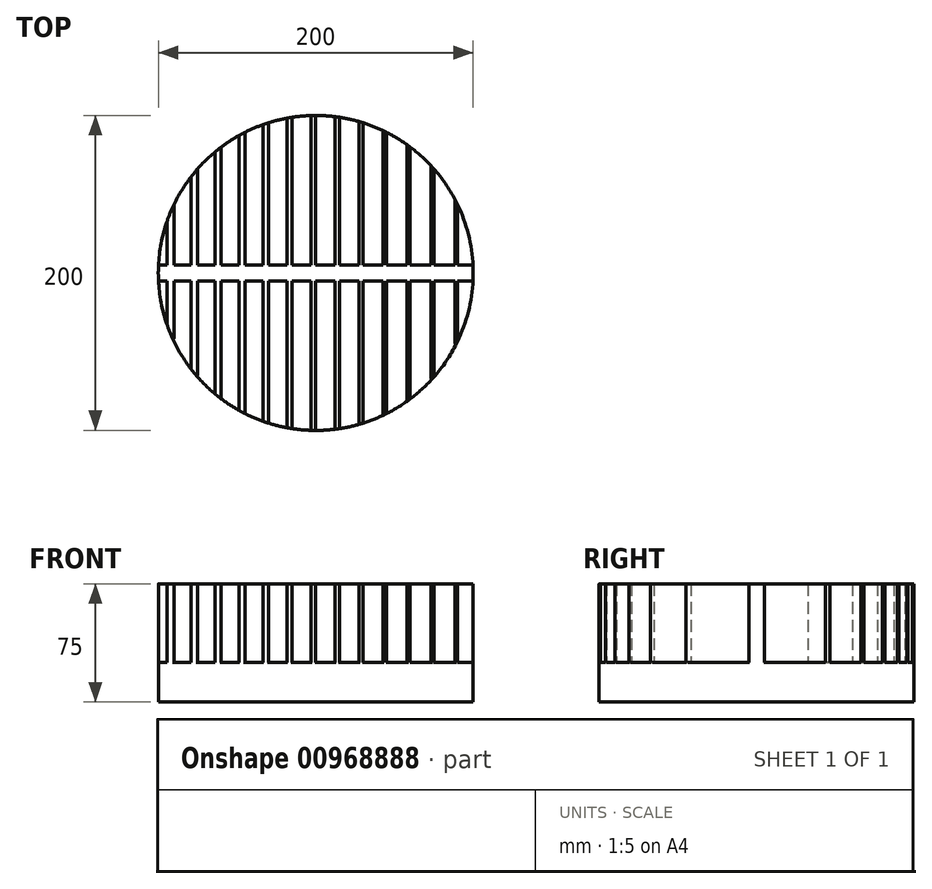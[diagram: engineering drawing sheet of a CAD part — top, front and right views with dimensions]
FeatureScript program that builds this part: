
annotation { "Feature Type Name" : "Feature", "Feature Type Description" : "" }
export const myFeature = defineFeature(function(context is Context, id is Id, definition is map)
    precondition{}
    {
        {
            var Q0;
            Q0=qCreatedBy(makeId("Top.planeOp"),FACE);
            var sketch = newSketch(context, id + "F0", { "sketchPlane" : qUnion([Q0])});
            skCircle(sketch, "E0", {"center": v(0, 0) * mm, "radius": 100 * mm});
            skLineSegment(sketch, "E1", {"start": v(-153.58, 0) * mm, "end": v(193.93, 0) * mm});
            skLineSegment(sketch, "E2", {"start": v(0, 104.63) * mm, "end": v(0, -103.63) * mm});
            skLineSegment(sketch, "E3.1.0.0", {"start": v(15, 104.63) * mm, "end": v(15, -103.63) * mm});
            skLineSegment(sketch, "E3.2.0.0", {"start": v(30, 104.63) * mm, "end": v(30, -103.63) * mm});
            skLineSegment(sketch, "E3.3.0.0", {"start": v(45, 104.63) * mm, "end": v(45, -103.63) * mm});
            skLineSegment(sketch, "E3.4.0.0", {"start": v(60, 104.63) * mm, "end": v(60, -103.63) * mm});
            skLineSegment(sketch, "E3.5.0.0", {"start": v(75, 104.63) * mm, "end": v(75, -103.63) * mm});
            skLineSegment(sketch, "E3.6.0.0", {"start": v(90, 104.63) * mm, "end": v(90, -103.63) * mm});
            skLineSegment(sketch, "E3.direction1", {"start": v(0, -103.63) * mm, "end": v(15, -103.63) * mm, "construction": true});
            skLineSegment(sketch, "E4.MirrorCS", {"start": v(-15, 104.63) * mm, "end": v(-15, -103.63) * mm});
            skLineSegment(sketch, "E5.MirrorCS", {"start": v(-30, 104.63) * mm, "end": v(-30, -103.63) * mm});
            skLineSegment(sketch, "E6.MirrorCS", {"start": v(-45, 104.63) * mm, "end": v(-45, -103.63) * mm});
            skLineSegment(sketch, "E7.MirrorCS", {"start": v(-60, 104.63) * mm, "end": v(-60, -103.63) * mm});
            skLineSegment(sketch, "E8.MirrorCS", {"start": v(-75, 104.63) * mm, "end": v(-75, -103.63) * mm});
            skLineSegment(sketch, "E9.MirrorCS", {"start": v(-90, 104.63) * mm, "end": v(-90, -103.63) * mm});
            skLineSegment(sketch, "E10.0", {"start": v(88.5, 104.63) * mm, "end": v(88.5, -103.63) * mm});
            skLineSegment(sketch, "E11.0", {"start": v(73.25, 104.63) * mm, "end": v(73.25, -103.63) * mm});
            skLineSegment(sketch, "E12.0", {"start": v(58, 104.63) * mm, "end": v(58, -103.63) * mm});
            skLineSegment(sketch, "E13.0", {"start": v(42.75, 104.63) * mm, "end": v(42.75, -103.63) * mm});
            skLineSegment(sketch, "E14.0", {"start": v(27.5, 104.63) * mm, "end": v(27.5, -103.63) * mm});
            skLineSegment(sketch, "E15.0", {"start": v(12.25, 104.63) * mm, "end": v(12.25, -103.63) * mm});
            skLineSegment(sketch, "E16.0", {"start": v(-3, 104.63) * mm, "end": v(-3, -103.63) * mm});
            skLineSegment(sketch, "E17.0", {"start": v(-18.25, 104.63) * mm, "end": v(-18.25, -103.63) * mm});
            skLineSegment(sketch, "E18.0", {"start": v(-33.5, 104.63) * mm, "end": v(-33.5, -103.63) * mm});
            skLineSegment(sketch, "E19.0", {"start": v(-48.75, 104.63) * mm, "end": v(-48.75, -103.63) * mm});
            skLineSegment(sketch, "E20.0", {"start": v(-64, 104.63) * mm, "end": v(-64, -103.63) * mm});
            skLineSegment(sketch, "E21.0", {"start": v(-79.25, 104.63) * mm, "end": v(-79.25, -103.63) * mm});
            skLineSegment(sketch, "E22.0", {"start": v(-94.5, 104.63) * mm, "end": v(-94.5, -103.63) * mm});
            skLineSegment(sketch, "E23.bottom", {"start": v(-150, 5) * mm, "end": v(150, 5) * mm});
            skLineSegment(sketch, "E23.top", {"start": v(-150, -5) * mm, "end": v(150, -5) * mm});
            skLineSegment(sketch, "E23.left", {"start": v(-150, 5) * mm, "end": v(-150, -5) * mm});
            skLineSegment(sketch, "E23.right", {"start": v(150, 5) * mm, "end": v(150, -5) * mm});
            skSolve(sketch);
        }
        {
            var Q0;
            {var subQ0=sQuery(id+"F0.wireOp",EDGE,"E22.0");var subQ1=sQuery(id+"F0.wireOp",EDGE,"E0");var subQ2=makeQuery(id+"F0.imprint","INTERSECT",VERTEX,{"disambiguationData":[OD(1.0)],"derivedFrom":[subQ1,subQ0]});Q0=makeQuery(id+"F0.imprint","IMPRINT",FACE,{"disambiguationData":[TD([[makeQuery(id+"F0.imprint","IMPRINT",EDGE,{"disambiguationData":[TD([[subQ2,1.0]])],"derivedFrom":subQ1}),1.0]])]});}
            var Q1;
            {var subQ0=sQuery(id+"F0.wireOp",EDGE,"E23.top");var subQ1=sQuery(id+"F0.wireOp",EDGE,"E0");var subQ2=makeQuery(id+"F0.imprint","INTERSECT",VERTEX,{"disambiguationData":[OD(0.0)],"derivedFrom":[subQ1,subQ0]});Q1=makeQuery(id+"F0.imprint","IMPRINT",FACE,{"disambiguationData":[TD([[makeQuery(id+"F0.imprint","IMPRINT",EDGE,{"disambiguationData":[TD([[subQ2,1.0]])],"derivedFrom":subQ1}),1.0]])]});}
            var Q2;
            {var subQ0=sQuery(id+"F0.wireOp",EDGE,"E23.bottom");var subQ1=sQuery(id+"F0.wireOp",EDGE,"E0");var subQ2=makeQuery(id+"F0.imprint","INTERSECT",VERTEX,{"disambiguationData":[OD(1.0)],"derivedFrom":[subQ1,subQ0]});Q2=makeQuery(id+"F0.imprint","IMPRINT",FACE,{"disambiguationData":[TD([[makeQuery(id+"F0.imprint","IMPRINT",EDGE,{"disambiguationData":[TD([[subQ2,-1.0]])],"derivedFrom":subQ1}),1.0]])]});}
            var Q3;
            {var subQ0=sQuery(id+"F0.wireOp",EDGE,"E22.0");var subQ1=sQuery(id+"F0.wireOp",EDGE,"E0");var subQ2=makeQuery(id+"F0.imprint","INTERSECT",VERTEX,{"disambiguationData":[OD(0.0)],"derivedFrom":[subQ1,subQ0]});Q3=makeQuery(id+"F0.imprint","IMPRINT",FACE,{"disambiguationData":[TD([[makeQuery(id+"F0.imprint","IMPRINT",EDGE,{"disambiguationData":[TD([[subQ2,-1.0]])],"derivedFrom":subQ1}),1.0]])]});}
            var Q4;
            {var subQ0=sQuery(id+"F0.wireOp",EDGE,"E4.MirrorCS");var subQ1=sQuery(id+"F0.wireOp",EDGE,"E0");var subQ2=makeQuery(id+"F0.imprint","INTERSECT",VERTEX,{"disambiguationData":[OD(1.0)],"derivedFrom":[subQ1,subQ0]});Q4=makeQuery(id+"F0.imprint","IMPRINT",FACE,{"disambiguationData":[TD([[makeQuery(id+"F0.imprint","IMPRINT",EDGE,{"disambiguationData":[TD([[subQ2,-1.0]])],"derivedFrom":subQ1}),1.0]])]});}
            var Q5;
            {var subQ0=sQuery(id+"F0.wireOp",EDGE,"E5.MirrorCS");var subQ1=sQuery(id+"F0.wireOp",EDGE,"E0");var subQ2=makeQuery(id+"F0.imprint","INTERSECT",VERTEX,{"disambiguationData":[OD(0.0)],"derivedFrom":[subQ1,subQ0]});Q5=makeQuery(id+"F0.imprint","IMPRINT",FACE,{"disambiguationData":[TD([[makeQuery(id+"F0.imprint","IMPRINT",EDGE,{"disambiguationData":[TD([[subQ2,-1.0]])],"derivedFrom":subQ1}),1.0]])]});}
            var Q6;
            {var subQ0=sQuery(id+"F0.wireOp",EDGE,"E16.0");var subQ1=sQuery(id+"F0.wireOp",EDGE,"E0");var subQ2=makeQuery(id+"F0.imprint","INTERSECT",VERTEX,{"disambiguationData":[OD(0.0)],"derivedFrom":[subQ1,subQ0]});Q6=makeQuery(id+"F0.imprint","IMPRINT",FACE,{"disambiguationData":[TD([[makeQuery(id+"F0.imprint","IMPRINT",EDGE,{"disambiguationData":[TD([[subQ2,-1.0]])],"derivedFrom":subQ1}),1.0]])]});}
            var Q7;
            {var subQ0=sQuery(id+"F0.wireOp",EDGE,"E15.0");var subQ1=sQuery(id+"F0.wireOp",EDGE,"E0");var subQ2=makeQuery(id+"F0.imprint","INTERSECT",VERTEX,{"disambiguationData":[OD(1.0)],"derivedFrom":[subQ1,subQ0]});Q7=makeQuery(id+"F0.imprint","IMPRINT",FACE,{"disambiguationData":[TD([[makeQuery(id+"F0.imprint","IMPRINT",EDGE,{"disambiguationData":[TD([[subQ2,-1.0]])],"derivedFrom":subQ1}),1.0]])]});}
            var Q8;
            {var subQ0=sQuery(id+"F0.wireOp",EDGE,"E8.MirrorCS");var subQ1=sQuery(id+"F0.wireOp",EDGE,"E1");var subQ2=makeQuery(id+"F0.imprint","INTERSECT",VERTEX,{"derivedFrom":[subQ1,subQ0]});Q8=makeQuery(id+"F0.imprint","IMPRINT",FACE,{"disambiguationData":[TD([[makeQuery(id+"F0.imprint","IMPRINT",EDGE,{"disambiguationData":[TD([[subQ2,-1.0]])],"derivedFrom":subQ1}),-1.0]])]});}
            var Q9;
            {var subQ0=sQuery(id+"F0.wireOp",EDGE,"E17.0");var subQ1=sQuery(id+"F0.wireOp",EDGE,"E0");var subQ2=makeQuery(id+"F0.imprint","INTERSECT",VERTEX,{"disambiguationData":[OD(0.0)],"derivedFrom":[subQ1,subQ0]});Q9=makeQuery(id+"F0.imprint","IMPRINT",FACE,{"disambiguationData":[TD([[makeQuery(id+"F0.imprint","IMPRINT",EDGE,{"disambiguationData":[TD([[subQ2,-1.0]])],"derivedFrom":subQ1}),1.0]])]});}
            var Q10;
            {var subQ0=sQuery(id+"F0.wireOp",EDGE,"E8.MirrorCS");var subQ1=sQuery(id+"F0.wireOp",EDGE,"E1");var subQ2=makeQuery(id+"F0.imprint","INTERSECT",VERTEX,{"derivedFrom":[subQ1,subQ0]});Q10=makeQuery(id+"F0.imprint","IMPRINT",FACE,{"disambiguationData":[TD([[makeQuery(id+"F0.imprint","IMPRINT",EDGE,{"disambiguationData":[TD([[subQ2,1.0]])],"derivedFrom":subQ1}),-1.0]])]});}
            var Q11;
            {var subQ0=sQuery(id+"F0.wireOp",EDGE,"E3.3.0.0");var subQ1=sQuery(id+"F0.wireOp",EDGE,"E0");var subQ2=makeQuery(id+"F0.imprint","INTERSECT",VERTEX,{"disambiguationData":[OD(0.0)],"derivedFrom":[subQ1,subQ0]});Q11=makeQuery(id+"F0.imprint","IMPRINT",FACE,{"disambiguationData":[TD([[makeQuery(id+"F0.imprint","IMPRINT",EDGE,{"disambiguationData":[TD([[subQ2,-1.0]])],"derivedFrom":subQ1}),1.0]])]});}
            var Q12;
            {var subQ0=sQuery(id+"F0.wireOp",EDGE,"E17.0");var subQ1=sQuery(id+"F0.wireOp",EDGE,"E1");var subQ2=makeQuery(id+"F0.imprint","INTERSECT",VERTEX,{"derivedFrom":[subQ1,subQ0]});Q12=makeQuery(id+"F0.imprint","IMPRINT",FACE,{"disambiguationData":[TD([[makeQuery(id+"F0.imprint","IMPRINT",EDGE,{"disambiguationData":[TD([[subQ2,-1.0]])],"derivedFrom":subQ1}),1.0]])]});}
            var Q13;
            {var subQ0=sQuery(id+"F0.wireOp",EDGE,"E13.0");var subQ1=sQuery(id+"F0.wireOp",EDGE,"E0");var subQ2=makeQuery(id+"F0.imprint","INTERSECT",VERTEX,{"disambiguationData":[OD(0.0)],"derivedFrom":[subQ1,subQ0]});Q13=makeQuery(id+"F0.imprint","IMPRINT",FACE,{"disambiguationData":[TD([[makeQuery(id+"F0.imprint","IMPRINT",EDGE,{"disambiguationData":[TD([[subQ2,-1.0]])],"derivedFrom":subQ1}),1.0]])]});}
            var Q14;
            {var subQ0=sQuery(id+"F0.wireOp",EDGE,"E13.0");var subQ1=sQuery(id+"F0.wireOp",EDGE,"E1");var subQ2=makeQuery(id+"F0.imprint","INTERSECT",VERTEX,{"derivedFrom":[subQ1,subQ0]});Q14=makeQuery(id+"F0.imprint","IMPRINT",FACE,{"disambiguationData":[TD([[makeQuery(id+"F0.imprint","IMPRINT",EDGE,{"disambiguationData":[TD([[subQ2,-1.0]])],"derivedFrom":subQ1}),-1.0]])]});}
            var Q15;
            {var subQ0=sQuery(id+"F0.wireOp",EDGE,"E5.MirrorCS");var subQ1=sQuery(id+"F0.wireOp",EDGE,"E1");var subQ2=makeQuery(id+"F0.imprint","INTERSECT",VERTEX,{"derivedFrom":[subQ1,subQ0]});Q15=makeQuery(id+"F0.imprint","IMPRINT",FACE,{"disambiguationData":[TD([[makeQuery(id+"F0.imprint","IMPRINT",EDGE,{"disambiguationData":[TD([[subQ2,1.0]])],"derivedFrom":subQ1}),-1.0]])]});}
            var Q16;
            {var subQ0=sQuery(id+"F0.wireOp",EDGE,"E7.MirrorCS");var subQ1=sQuery(id+"F0.wireOp",EDGE,"E1");var subQ2=makeQuery(id+"F0.imprint","INTERSECT",VERTEX,{"derivedFrom":[subQ1,subQ0]});Q16=makeQuery(id+"F0.imprint","IMPRINT",FACE,{"disambiguationData":[TD([[makeQuery(id+"F0.imprint","IMPRINT",EDGE,{"disambiguationData":[TD([[subQ2,-1.0]])],"derivedFrom":subQ1}),-1.0]])]});}
            var Q17;
            {var subQ0=sQuery(id+"F0.wireOp",EDGE,"E3.2.0.0");var subQ1=sQuery(id+"F0.wireOp",EDGE,"E0");var subQ2=makeQuery(id+"F0.imprint","INTERSECT",VERTEX,{"disambiguationData":[OD(0.0)],"derivedFrom":[subQ1,subQ0]});Q17=makeQuery(id+"F0.imprint","IMPRINT",FACE,{"disambiguationData":[TD([[makeQuery(id+"F0.imprint","IMPRINT",EDGE,{"disambiguationData":[TD([[subQ2,-1.0]])],"derivedFrom":subQ1}),1.0]])]});}
            var Q18;
            {var subQ0=sQuery(id+"F0.wireOp",EDGE,"E15.0");var subQ1=sQuery(id+"F0.wireOp",EDGE,"E0");var subQ2=makeQuery(id+"F0.imprint","INTERSECT",VERTEX,{"disambiguationData":[OD(0.0)],"derivedFrom":[subQ1,subQ0]});Q18=makeQuery(id+"F0.imprint","IMPRINT",FACE,{"disambiguationData":[TD([[makeQuery(id+"F0.imprint","IMPRINT",EDGE,{"disambiguationData":[TD([[subQ2,1.0]])],"derivedFrom":subQ1}),1.0]])]});}
            var Q19;
            {var subQ0=sQuery(id+"F0.wireOp",EDGE,"E6.MirrorCS");var subQ1=sQuery(id+"F0.wireOp",EDGE,"E1");var subQ2=makeQuery(id+"F0.imprint","INTERSECT",VERTEX,{"derivedFrom":[subQ1,subQ0]});Q19=makeQuery(id+"F0.imprint","IMPRINT",FACE,{"disambiguationData":[TD([[makeQuery(id+"F0.imprint","IMPRINT",EDGE,{"disambiguationData":[TD([[subQ2,-1.0]])],"derivedFrom":subQ1}),1.0]])]});}
            var Q20;
            {var subQ0=sQuery(id+"F0.wireOp",EDGE,"E9.MirrorCS");var subQ1=sQuery(id+"F0.wireOp",EDGE,"E1");var subQ2=makeQuery(id+"F0.imprint","INTERSECT",VERTEX,{"derivedFrom":[subQ1,subQ0]});Q20=makeQuery(id+"F0.imprint","IMPRINT",FACE,{"disambiguationData":[TD([[makeQuery(id+"F0.imprint","IMPRINT",EDGE,{"disambiguationData":[TD([[subQ2,-1.0]])],"derivedFrom":subQ1}),1.0]])]});}
            var Q21;
            {var subQ0=sQuery(id+"F0.wireOp",EDGE,"E8.MirrorCS");var subQ1=sQuery(id+"F0.wireOp",EDGE,"E0");var subQ2=makeQuery(id+"F0.imprint","INTERSECT",VERTEX,{"disambiguationData":[OD(1.0)],"derivedFrom":[subQ1,subQ0]});Q21=makeQuery(id+"F0.imprint","IMPRINT",FACE,{"disambiguationData":[TD([[makeQuery(id+"F0.imprint","IMPRINT",EDGE,{"disambiguationData":[TD([[subQ2,-1.0]])],"derivedFrom":subQ1}),1.0]])]});}
            var Q22;
            {var subQ0=sQuery(id+"F0.wireOp",EDGE,"E9.MirrorCS");var subQ1=sQuery(id+"F0.wireOp",EDGE,"E1");var subQ2=makeQuery(id+"F0.imprint","INTERSECT",VERTEX,{"derivedFrom":[subQ1,subQ0]});Q22=makeQuery(id+"F0.imprint","IMPRINT",FACE,{"disambiguationData":[TD([[makeQuery(id+"F0.imprint","IMPRINT",EDGE,{"disambiguationData":[TD([[subQ2,1.0]])],"derivedFrom":subQ1}),-1.0]])]});}
            var Q23;
            {var subQ0=sQuery(id+"F0.wireOp",EDGE,"E3.3.0.0");var subQ1=sQuery(id+"F0.wireOp",EDGE,"E0");var subQ2=makeQuery(id+"F0.imprint","INTERSECT",VERTEX,{"disambiguationData":[OD(1.0)],"derivedFrom":[subQ1,subQ0]});Q23=makeQuery(id+"F0.imprint","IMPRINT",FACE,{"disambiguationData":[TD([[makeQuery(id+"F0.imprint","IMPRINT",EDGE,{"disambiguationData":[TD([[subQ2,-1.0]])],"derivedFrom":subQ1}),1.0]])]});}
            var Q24;
            {var subQ0=sQuery(id+"F0.wireOp",EDGE,"E7.MirrorCS");var subQ1=sQuery(id+"F0.wireOp",EDGE,"E1");var subQ2=makeQuery(id+"F0.imprint","INTERSECT",VERTEX,{"derivedFrom":[subQ1,subQ0]});Q24=makeQuery(id+"F0.imprint","IMPRINT",FACE,{"disambiguationData":[TD([[makeQuery(id+"F0.imprint","IMPRINT",EDGE,{"disambiguationData":[TD([[subQ2,1.0]])],"derivedFrom":subQ1}),-1.0]])]});}
            var Q25;
            {var subQ0=sQuery(id+"F0.wireOp",EDGE,"E3.1.0.0");var subQ1=sQuery(id+"F0.wireOp",EDGE,"E0");var subQ2=makeQuery(id+"F0.imprint","INTERSECT",VERTEX,{"disambiguationData":[OD(1.0)],"derivedFrom":[subQ1,subQ0]});Q25=makeQuery(id+"F0.imprint","IMPRINT",FACE,{"disambiguationData":[TD([[makeQuery(id+"F0.imprint","IMPRINT",EDGE,{"disambiguationData":[TD([[subQ2,-1.0]])],"derivedFrom":subQ1}),1.0]])]});}
            var Q26;
            {var subQ0=sQuery(id+"F0.wireOp",EDGE,"E6.MirrorCS");var subQ1=sQuery(id+"F0.wireOp",EDGE,"E1");var subQ2=makeQuery(id+"F0.imprint","INTERSECT",VERTEX,{"derivedFrom":[subQ1,subQ0]});Q26=makeQuery(id+"F0.imprint","IMPRINT",FACE,{"disambiguationData":[TD([[makeQuery(id+"F0.imprint","IMPRINT",EDGE,{"disambiguationData":[TD([[subQ2,1.0]])],"derivedFrom":subQ1}),-1.0]])]});}
            var Q27;
            {var subQ0=sQuery(id+"F0.wireOp",EDGE,"E11.0");var subQ1=sQuery(id+"F0.wireOp",EDGE,"E0");var subQ2=makeQuery(id+"F0.imprint","INTERSECT",VERTEX,{"disambiguationData":[OD(0.0)],"derivedFrom":[subQ1,subQ0]});Q27=makeQuery(id+"F0.imprint","IMPRINT",FACE,{"disambiguationData":[TD([[makeQuery(id+"F0.imprint","IMPRINT",EDGE,{"disambiguationData":[TD([[subQ2,-1.0]])],"derivedFrom":subQ1}),1.0]])]});}
            var Q28;
            {var subQ0=sQuery(id+"F0.wireOp",EDGE,"E17.0");var subQ1=sQuery(id+"F0.wireOp",EDGE,"E0");var subQ2=makeQuery(id+"F0.imprint","INTERSECT",VERTEX,{"disambiguationData":[OD(1.0)],"derivedFrom":[subQ1,subQ0]});Q28=makeQuery(id+"F0.imprint","IMPRINT",FACE,{"disambiguationData":[TD([[makeQuery(id+"F0.imprint","IMPRINT",EDGE,{"disambiguationData":[TD([[subQ2,-1.0]])],"derivedFrom":subQ1}),1.0]])]});}
            var Q29;
            {var subQ0=sQuery(id+"F0.wireOp",EDGE,"E12.0");var subQ1=sQuery(id+"F0.wireOp",EDGE,"E1");var subQ2=makeQuery(id+"F0.imprint","INTERSECT",VERTEX,{"derivedFrom":[subQ1,subQ0]});Q29=makeQuery(id+"F0.imprint","IMPRINT",FACE,{"disambiguationData":[TD([[makeQuery(id+"F0.imprint","IMPRINT",EDGE,{"disambiguationData":[TD([[subQ2,-1.0]])],"derivedFrom":subQ1}),1.0]])]});}
            var Q30;
            {var subQ0=sQuery(id+"F0.wireOp",EDGE,"E10.0");var subQ1=sQuery(id+"F0.wireOp",EDGE,"E1");var subQ2=makeQuery(id+"F0.imprint","INTERSECT",VERTEX,{"derivedFrom":[subQ1,subQ0]});Q30=makeQuery(id+"F0.imprint","IMPRINT",FACE,{"disambiguationData":[TD([[makeQuery(id+"F0.imprint","IMPRINT",EDGE,{"disambiguationData":[TD([[subQ2,1.0]])],"derivedFrom":subQ1}),1.0]])]});}
            var Q31;
            {var subQ0=sQuery(id+"F0.wireOp",EDGE,"E10.0");var subQ1=sQuery(id+"F0.wireOp",EDGE,"E0");var subQ2=makeQuery(id+"F0.imprint","INTERSECT",VERTEX,{"disambiguationData":[OD(1.0)],"derivedFrom":[subQ1,subQ0]});Q31=makeQuery(id+"F0.imprint","IMPRINT",FACE,{"disambiguationData":[TD([[makeQuery(id+"F0.imprint","IMPRINT",EDGE,{"disambiguationData":[TD([[subQ2,-1.0]])],"derivedFrom":subQ1}),1.0]])]});}
            var Q32;
            {var subQ0=sQuery(id+"F0.wireOp",EDGE,"E2");var subQ1=sQuery(id+"F0.wireOp",EDGE,"E1");var subQ2=makeQuery(id+"F0.imprint","INTERSECT",VERTEX,{"derivedFrom":[subQ1,subQ0]});Q32=makeQuery(id+"F0.imprint","IMPRINT",FACE,{"disambiguationData":[TD([[makeQuery(id+"F0.imprint","IMPRINT",EDGE,{"disambiguationData":[TD([[subQ2,-1.0]])],"derivedFrom":subQ1}),-1.0]])]});}
            var Q33;
            {var subQ0=sQuery(id+"F0.wireOp",EDGE,"E2");var subQ1=sQuery(id+"F0.wireOp",EDGE,"E0");var subQ2=makeQuery(id+"F0.imprint","INTERSECT",VERTEX,{"disambiguationData":[OD(1.0)],"derivedFrom":[subQ1,subQ0]});Q33=makeQuery(id+"F0.imprint","IMPRINT",FACE,{"disambiguationData":[TD([[makeQuery(id+"F0.imprint","IMPRINT",EDGE,{"disambiguationData":[TD([[subQ2,-1.0]])],"derivedFrom":subQ1}),1.0]])]});}
            var Q34;
            {var subQ0=sQuery(id+"F0.wireOp",EDGE,"E2");var subQ1=sQuery(id+"F0.wireOp",EDGE,"E0");var subQ2=makeQuery(id+"F0.imprint","INTERSECT",VERTEX,{"disambiguationData":[OD(0.0)],"derivedFrom":[subQ1,subQ0]});Q34=makeQuery(id+"F0.imprint","IMPRINT",FACE,{"disambiguationData":[TD([[makeQuery(id+"F0.imprint","IMPRINT",EDGE,{"disambiguationData":[TD([[subQ2,-1.0]])],"derivedFrom":subQ1}),1.0]])]});}
            var Q35;
            {var subQ0=sQuery(id+"F0.wireOp",EDGE,"E3.6.0.0");var subQ1=sQuery(id+"F0.wireOp",EDGE,"E0");var subQ2=makeQuery(id+"F0.imprint","INTERSECT",VERTEX,{"disambiguationData":[OD(1.0)],"derivedFrom":[subQ1,subQ0]});Q35=makeQuery(id+"F0.imprint","IMPRINT",FACE,{"disambiguationData":[TD([[makeQuery(id+"F0.imprint","IMPRINT",EDGE,{"disambiguationData":[TD([[subQ2,-1.0]])],"derivedFrom":subQ1}),1.0]])]});}
            var Q36;
            {var subQ0=sQuery(id+"F0.wireOp",EDGE,"E11.0");var subQ1=sQuery(id+"F0.wireOp",EDGE,"E1");var subQ2=makeQuery(id+"F0.imprint","INTERSECT",VERTEX,{"derivedFrom":[subQ1,subQ0]});Q36=makeQuery(id+"F0.imprint","IMPRINT",FACE,{"disambiguationData":[TD([[makeQuery(id+"F0.imprint","IMPRINT",EDGE,{"disambiguationData":[TD([[subQ2,-1.0]])],"derivedFrom":subQ1}),1.0]])]});}
            var Q37;
            {var subQ0=sQuery(id+"F0.wireOp",EDGE,"E21.0");var subQ1=sQuery(id+"F0.wireOp",EDGE,"E0");var subQ2=makeQuery(id+"F0.imprint","INTERSECT",VERTEX,{"disambiguationData":[OD(0.0)],"derivedFrom":[subQ1,subQ0]});Q37=makeQuery(id+"F0.imprint","IMPRINT",FACE,{"disambiguationData":[TD([[makeQuery(id+"F0.imprint","IMPRINT",EDGE,{"disambiguationData":[TD([[subQ2,-1.0]])],"derivedFrom":subQ1}),1.0]])]});}
            var Q38;
            {var subQ0=sQuery(id+"F0.wireOp",EDGE,"E20.0");var subQ1=sQuery(id+"F0.wireOp",EDGE,"E0");var subQ2=makeQuery(id+"F0.imprint","INTERSECT",VERTEX,{"disambiguationData":[OD(1.0)],"derivedFrom":[subQ1,subQ0]});Q38=makeQuery(id+"F0.imprint","IMPRINT",FACE,{"disambiguationData":[TD([[makeQuery(id+"F0.imprint","IMPRINT",EDGE,{"disambiguationData":[TD([[subQ2,-1.0]])],"derivedFrom":subQ1}),1.0]])]});}
            var Q39;
            {var subQ0=sQuery(id+"F0.wireOp",EDGE,"E19.0");var subQ1=sQuery(id+"F0.wireOp",EDGE,"E0");var subQ2=makeQuery(id+"F0.imprint","INTERSECT",VERTEX,{"disambiguationData":[OD(0.0)],"derivedFrom":[subQ1,subQ0]});Q39=makeQuery(id+"F0.imprint","IMPRINT",FACE,{"disambiguationData":[TD([[makeQuery(id+"F0.imprint","IMPRINT",EDGE,{"disambiguationData":[TD([[subQ2,-1.0]])],"derivedFrom":subQ1}),1.0]])]});}
            var Q40;
            {var subQ0=sQuery(id+"F0.wireOp",EDGE,"E13.0");var subQ1=sQuery(id+"F0.wireOp",EDGE,"E0");var subQ2=makeQuery(id+"F0.imprint","INTERSECT",VERTEX,{"disambiguationData":[OD(1.0)],"derivedFrom":[subQ1,subQ0]});Q40=makeQuery(id+"F0.imprint","IMPRINT",FACE,{"disambiguationData":[TD([[makeQuery(id+"F0.imprint","IMPRINT",EDGE,{"disambiguationData":[TD([[subQ2,-1.0]])],"derivedFrom":subQ1}),1.0]])]});}
            var Q41;
            {var subQ0=sQuery(id+"F0.wireOp",EDGE,"E3.4.0.0");var subQ1=sQuery(id+"F0.wireOp",EDGE,"E0");var subQ2=makeQuery(id+"F0.imprint","INTERSECT",VERTEX,{"disambiguationData":[OD(1.0)],"derivedFrom":[subQ1,subQ0]});Q41=makeQuery(id+"F0.imprint","IMPRINT",FACE,{"disambiguationData":[TD([[makeQuery(id+"F0.imprint","IMPRINT",EDGE,{"disambiguationData":[TD([[subQ2,-1.0]])],"derivedFrom":subQ1}),1.0]])]});}
            var Q42;
            {var subQ0=sQuery(id+"F0.wireOp",EDGE,"E7.MirrorCS");var subQ1=sQuery(id+"F0.wireOp",EDGE,"E1");var subQ2=makeQuery(id+"F0.imprint","INTERSECT",VERTEX,{"derivedFrom":[subQ1,subQ0]});Q42=makeQuery(id+"F0.imprint","IMPRINT",FACE,{"disambiguationData":[TD([[makeQuery(id+"F0.imprint","IMPRINT",EDGE,{"disambiguationData":[TD([[subQ2,1.0]])],"derivedFrom":subQ1}),1.0]])]});}
            var Q43;
            {var subQ0=sQuery(id+"F0.wireOp",EDGE,"E5.MirrorCS");var subQ1=sQuery(id+"F0.wireOp",EDGE,"E1");var subQ2=makeQuery(id+"F0.imprint","INTERSECT",VERTEX,{"derivedFrom":[subQ1,subQ0]});Q43=makeQuery(id+"F0.imprint","IMPRINT",FACE,{"disambiguationData":[TD([[makeQuery(id+"F0.imprint","IMPRINT",EDGE,{"disambiguationData":[TD([[subQ2,-1.0]])],"derivedFrom":subQ1}),-1.0]])]});}
            var Q44;
            {var subQ0=sQuery(id+"F0.wireOp",EDGE,"E12.0");var subQ1=sQuery(id+"F0.wireOp",EDGE,"E0");var subQ2=makeQuery(id+"F0.imprint","INTERSECT",VERTEX,{"disambiguationData":[OD(1.0)],"derivedFrom":[subQ1,subQ0]});Q44=makeQuery(id+"F0.imprint","IMPRINT",FACE,{"disambiguationData":[TD([[makeQuery(id+"F0.imprint","IMPRINT",EDGE,{"disambiguationData":[TD([[subQ2,-1.0]])],"derivedFrom":subQ1}),1.0]])]});}
            var Q45;
            {var subQ0=sQuery(id+"F0.wireOp",EDGE,"E7.MirrorCS");var subQ1=sQuery(id+"F0.wireOp",EDGE,"E0");var subQ2=makeQuery(id+"F0.imprint","INTERSECT",VERTEX,{"disambiguationData":[OD(1.0)],"derivedFrom":[subQ1,subQ0]});Q45=makeQuery(id+"F0.imprint","IMPRINT",FACE,{"disambiguationData":[TD([[makeQuery(id+"F0.imprint","IMPRINT",EDGE,{"disambiguationData":[TD([[subQ2,-1.0]])],"derivedFrom":subQ1}),1.0]])]});}
            var Q46;
            {var subQ0=sQuery(id+"F0.wireOp",EDGE,"E12.0");var subQ1=sQuery(id+"F0.wireOp",EDGE,"E1");var subQ2=makeQuery(id+"F0.imprint","INTERSECT",VERTEX,{"derivedFrom":[subQ1,subQ0]});Q46=makeQuery(id+"F0.imprint","IMPRINT",FACE,{"disambiguationData":[TD([[makeQuery(id+"F0.imprint","IMPRINT",EDGE,{"disambiguationData":[TD([[subQ2,1.0]])],"derivedFrom":subQ1}),-1.0]])]});}
            var Q47;
            {var subQ0=sQuery(id+"F0.wireOp",EDGE,"E14.0");var subQ1=sQuery(id+"F0.wireOp",EDGE,"E0");var subQ2=makeQuery(id+"F0.imprint","INTERSECT",VERTEX,{"disambiguationData":[OD(0.0)],"derivedFrom":[subQ1,subQ0]});Q47=makeQuery(id+"F0.imprint","IMPRINT",FACE,{"disambiguationData":[TD([[makeQuery(id+"F0.imprint","IMPRINT",EDGE,{"disambiguationData":[TD([[subQ2,-1.0]])],"derivedFrom":subQ1}),1.0]])]});}
            var Q48;
            {var subQ0=sQuery(id+"F0.wireOp",EDGE,"E3.6.0.0");var subQ1=sQuery(id+"F0.wireOp",EDGE,"E1");var subQ2=makeQuery(id+"F0.imprint","INTERSECT",VERTEX,{"derivedFrom":[subQ1,subQ0]});Q48=makeQuery(id+"F0.imprint","IMPRINT",FACE,{"disambiguationData":[TD([[makeQuery(id+"F0.imprint","IMPRINT",EDGE,{"disambiguationData":[TD([[subQ2,1.0]])],"derivedFrom":subQ1}),-1.0]])]});}
            var Q49;
            {var subQ0=sQuery(id+"F0.wireOp",EDGE,"E8.MirrorCS");var subQ1=sQuery(id+"F0.wireOp",EDGE,"E0");var subQ2=makeQuery(id+"F0.imprint","INTERSECT",VERTEX,{"disambiguationData":[OD(0.0)],"derivedFrom":[subQ1,subQ0]});Q49=makeQuery(id+"F0.imprint","IMPRINT",FACE,{"disambiguationData":[TD([[makeQuery(id+"F0.imprint","IMPRINT",EDGE,{"disambiguationData":[TD([[subQ2,-1.0]])],"derivedFrom":subQ1}),1.0]])]});}
            var Q50;
            {var subQ0=sQuery(id+"F0.wireOp",EDGE,"E6.MirrorCS");var subQ1=sQuery(id+"F0.wireOp",EDGE,"E1");var subQ2=makeQuery(id+"F0.imprint","INTERSECT",VERTEX,{"derivedFrom":[subQ1,subQ0]});Q50=makeQuery(id+"F0.imprint","IMPRINT",FACE,{"disambiguationData":[TD([[makeQuery(id+"F0.imprint","IMPRINT",EDGE,{"disambiguationData":[TD([[subQ2,-1.0]])],"derivedFrom":subQ1}),-1.0]])]});}
            var Q51;
            {var subQ0=sQuery(id+"F0.wireOp",EDGE,"E22.0");var subQ1=sQuery(id+"F0.wireOp",EDGE,"E0");var subQ2=makeQuery(id+"F0.imprint","INTERSECT",VERTEX,{"disambiguationData":[OD(1.0)],"derivedFrom":[subQ1,subQ0]});Q51=makeQuery(id+"F0.imprint","IMPRINT",FACE,{"disambiguationData":[TD([[makeQuery(id+"F0.imprint","IMPRINT",EDGE,{"disambiguationData":[TD([[subQ2,-1.0]])],"derivedFrom":subQ1}),1.0]])]});}
            var Q52;
            {var subQ0=sQuery(id+"F0.wireOp",EDGE,"E11.0");var subQ1=sQuery(id+"F0.wireOp",EDGE,"E1");var subQ2=makeQuery(id+"F0.imprint","INTERSECT",VERTEX,{"derivedFrom":[subQ1,subQ0]});Q52=makeQuery(id+"F0.imprint","IMPRINT",FACE,{"disambiguationData":[TD([[makeQuery(id+"F0.imprint","IMPRINT",EDGE,{"disambiguationData":[TD([[subQ2,-1.0]])],"derivedFrom":subQ1}),-1.0]])]});}
            var Q53;
            {var subQ0=sQuery(id+"F0.wireOp",EDGE,"E3.2.0.0");var subQ1=sQuery(id+"F0.wireOp",EDGE,"E1");var subQ2=makeQuery(id+"F0.imprint","INTERSECT",VERTEX,{"derivedFrom":[subQ1,subQ0]});Q53=makeQuery(id+"F0.imprint","IMPRINT",FACE,{"disambiguationData":[TD([[makeQuery(id+"F0.imprint","IMPRINT",EDGE,{"disambiguationData":[TD([[subQ2,1.0]])],"derivedFrom":subQ1}),-1.0]])]});}
            var Q54;
            {var subQ0=sQuery(id+"F0.wireOp",EDGE,"E11.0");var subQ1=sQuery(id+"F0.wireOp",EDGE,"E1");var subQ2=makeQuery(id+"F0.imprint","INTERSECT",VERTEX,{"derivedFrom":[subQ1,subQ0]});Q54=makeQuery(id+"F0.imprint","IMPRINT",FACE,{"disambiguationData":[TD([[makeQuery(id+"F0.imprint","IMPRINT",EDGE,{"disambiguationData":[TD([[subQ2,1.0]])],"derivedFrom":subQ1}),1.0]])]});}
            var Q55;
            {var subQ0=sQuery(id+"F0.wireOp",EDGE,"E7.MirrorCS");var subQ1=sQuery(id+"F0.wireOp",EDGE,"E1");var subQ2=makeQuery(id+"F0.imprint","INTERSECT",VERTEX,{"derivedFrom":[subQ1,subQ0]});Q55=makeQuery(id+"F0.imprint","IMPRINT",FACE,{"disambiguationData":[TD([[makeQuery(id+"F0.imprint","IMPRINT",EDGE,{"disambiguationData":[TD([[subQ2,-1.0]])],"derivedFrom":subQ1}),1.0]])]});}
            var Q56;
            {var subQ0=sQuery(id+"F0.wireOp",EDGE,"E18.0");var subQ1=sQuery(id+"F0.wireOp",EDGE,"E0");var subQ2=makeQuery(id+"F0.imprint","INTERSECT",VERTEX,{"disambiguationData":[OD(1.0)],"derivedFrom":[subQ1,subQ0]});Q56=makeQuery(id+"F0.imprint","IMPRINT",FACE,{"disambiguationData":[TD([[makeQuery(id+"F0.imprint","IMPRINT",EDGE,{"disambiguationData":[TD([[subQ2,-1.0]])],"derivedFrom":subQ1}),1.0]])]});}
            var Q57;
            {var subQ0=sQuery(id+"F0.wireOp",EDGE,"E3.2.0.0");var subQ1=sQuery(id+"F0.wireOp",EDGE,"E1");var subQ2=makeQuery(id+"F0.imprint","INTERSECT",VERTEX,{"derivedFrom":[subQ1,subQ0]});Q57=makeQuery(id+"F0.imprint","IMPRINT",FACE,{"disambiguationData":[TD([[makeQuery(id+"F0.imprint","IMPRINT",EDGE,{"disambiguationData":[TD([[subQ2,-1.0]])],"derivedFrom":subQ1}),-1.0]])]});}
            var Q58;
            {var subQ0=sQuery(id+"F0.wireOp",EDGE,"E11.0");var subQ1=sQuery(id+"F0.wireOp",EDGE,"E1");var subQ2=makeQuery(id+"F0.imprint","INTERSECT",VERTEX,{"derivedFrom":[subQ1,subQ0]});Q58=makeQuery(id+"F0.imprint","IMPRINT",FACE,{"disambiguationData":[TD([[makeQuery(id+"F0.imprint","IMPRINT",EDGE,{"disambiguationData":[TD([[subQ2,1.0]])],"derivedFrom":subQ1}),-1.0]])]});}
            var Q59;
            {var subQ0=sQuery(id+"F0.wireOp",EDGE,"E12.0");var subQ1=sQuery(id+"F0.wireOp",EDGE,"E1");var subQ2=makeQuery(id+"F0.imprint","INTERSECT",VERTEX,{"derivedFrom":[subQ1,subQ0]});Q59=makeQuery(id+"F0.imprint","IMPRINT",FACE,{"disambiguationData":[TD([[makeQuery(id+"F0.imprint","IMPRINT",EDGE,{"disambiguationData":[TD([[subQ2,-1.0]])],"derivedFrom":subQ1}),-1.0]])]});}
            var Q60;
            {var subQ0=sQuery(id+"F0.wireOp",EDGE,"E12.0");var subQ1=sQuery(id+"F0.wireOp",EDGE,"E0");var subQ2=makeQuery(id+"F0.imprint","INTERSECT",VERTEX,{"disambiguationData":[OD(0.0)],"derivedFrom":[subQ1,subQ0]});Q60=makeQuery(id+"F0.imprint","IMPRINT",FACE,{"disambiguationData":[TD([[makeQuery(id+"F0.imprint","IMPRINT",EDGE,{"disambiguationData":[TD([[subQ2,1.0]])],"derivedFrom":subQ1}),1.0]])]});}
            var Q61;
            {var subQ0=sQuery(id+"F0.wireOp",EDGE,"E13.0");var subQ1=sQuery(id+"F0.wireOp",EDGE,"E1");var subQ2=makeQuery(id+"F0.imprint","INTERSECT",VERTEX,{"derivedFrom":[subQ1,subQ0]});Q61=makeQuery(id+"F0.imprint","IMPRINT",FACE,{"disambiguationData":[TD([[makeQuery(id+"F0.imprint","IMPRINT",EDGE,{"disambiguationData":[TD([[subQ2,-1.0]])],"derivedFrom":subQ1}),1.0]])]});}
            var Q62;
            {var subQ0=sQuery(id+"F0.wireOp",EDGE,"E6.MirrorCS");var subQ1=sQuery(id+"F0.wireOp",EDGE,"E0");var subQ2=makeQuery(id+"F0.imprint","INTERSECT",VERTEX,{"disambiguationData":[OD(1.0)],"derivedFrom":[subQ1,subQ0]});Q62=makeQuery(id+"F0.imprint","IMPRINT",FACE,{"disambiguationData":[TD([[makeQuery(id+"F0.imprint","IMPRINT",EDGE,{"disambiguationData":[TD([[subQ2,-1.0]])],"derivedFrom":subQ1}),1.0]])]});}
            var Q63;
            {var subQ0=sQuery(id+"F0.wireOp",EDGE,"E6.MirrorCS");var subQ1=sQuery(id+"F0.wireOp",EDGE,"E1");var subQ2=makeQuery(id+"F0.imprint","INTERSECT",VERTEX,{"derivedFrom":[subQ1,subQ0]});Q63=makeQuery(id+"F0.imprint","IMPRINT",FACE,{"disambiguationData":[TD([[makeQuery(id+"F0.imprint","IMPRINT",EDGE,{"disambiguationData":[TD([[subQ2,1.0]])],"derivedFrom":subQ1}),1.0]])]});}
            var Q64;
            {var subQ0=sQuery(id+"F0.wireOp",EDGE,"E20.0");var subQ1=sQuery(id+"F0.wireOp",EDGE,"E0");var subQ2=makeQuery(id+"F0.imprint","INTERSECT",VERTEX,{"disambiguationData":[OD(0.0)],"derivedFrom":[subQ1,subQ0]});Q64=makeQuery(id+"F0.imprint","IMPRINT",FACE,{"disambiguationData":[TD([[makeQuery(id+"F0.imprint","IMPRINT",EDGE,{"disambiguationData":[TD([[subQ2,1.0]])],"derivedFrom":subQ1}),1.0]])]});}
            var Q65;
            {var subQ0=sQuery(id+"F0.wireOp",EDGE,"E9.MirrorCS");var subQ1=sQuery(id+"F0.wireOp",EDGE,"E0");var subQ2=makeQuery(id+"F0.imprint","INTERSECT",VERTEX,{"disambiguationData":[OD(1.0)],"derivedFrom":[subQ1,subQ0]});Q65=makeQuery(id+"F0.imprint","IMPRINT",FACE,{"disambiguationData":[TD([[makeQuery(id+"F0.imprint","IMPRINT",EDGE,{"disambiguationData":[TD([[subQ2,-1.0]])],"derivedFrom":subQ1}),1.0]])]});}
            var Q66;
            {var subQ0=sQuery(id+"F0.wireOp",EDGE,"E17.0");var subQ1=sQuery(id+"F0.wireOp",EDGE,"E1");var subQ2=makeQuery(id+"F0.imprint","INTERSECT",VERTEX,{"derivedFrom":[subQ1,subQ0]});Q66=makeQuery(id+"F0.imprint","IMPRINT",FACE,{"disambiguationData":[TD([[makeQuery(id+"F0.imprint","IMPRINT",EDGE,{"disambiguationData":[TD([[subQ2,-1.0]])],"derivedFrom":subQ1}),-1.0]])]});}
            var Q67;
            {var subQ0=sQuery(id+"F0.wireOp",EDGE,"E15.0");var subQ1=sQuery(id+"F0.wireOp",EDGE,"E0");var subQ2=makeQuery(id+"F0.imprint","INTERSECT",VERTEX,{"disambiguationData":[OD(0.0)],"derivedFrom":[subQ1,subQ0]});Q67=makeQuery(id+"F0.imprint","IMPRINT",FACE,{"disambiguationData":[TD([[makeQuery(id+"F0.imprint","IMPRINT",EDGE,{"disambiguationData":[TD([[subQ2,-1.0]])],"derivedFrom":subQ1}),1.0]])]});}
            var Q68;
            {var subQ0=sQuery(id+"F0.wireOp",EDGE,"E3.6.0.0");var subQ1=sQuery(id+"F0.wireOp",EDGE,"E0");var subQ2=makeQuery(id+"F0.imprint","INTERSECT",VERTEX,{"disambiguationData":[OD(0.0)],"derivedFrom":[subQ1,subQ0]});Q68=makeQuery(id+"F0.imprint","IMPRINT",FACE,{"disambiguationData":[TD([[makeQuery(id+"F0.imprint","IMPRINT",EDGE,{"disambiguationData":[TD([[subQ2,1.0]])],"derivedFrom":subQ1}),1.0]])]});}
            var Q69;
            {var subQ0=sQuery(id+"F0.wireOp",EDGE,"E9.MirrorCS");var subQ1=sQuery(id+"F0.wireOp",EDGE,"E1");var subQ2=makeQuery(id+"F0.imprint","INTERSECT",VERTEX,{"derivedFrom":[subQ1,subQ0]});Q69=makeQuery(id+"F0.imprint","IMPRINT",FACE,{"disambiguationData":[TD([[makeQuery(id+"F0.imprint","IMPRINT",EDGE,{"disambiguationData":[TD([[subQ2,-1.0]])],"derivedFrom":subQ1}),-1.0]])]});}
            var Q70;
            {var subQ0=sQuery(id+"F0.wireOp",EDGE,"E8.MirrorCS");var subQ1=sQuery(id+"F0.wireOp",EDGE,"E1");var subQ2=makeQuery(id+"F0.imprint","INTERSECT",VERTEX,{"derivedFrom":[subQ1,subQ0]});Q70=makeQuery(id+"F0.imprint","IMPRINT",FACE,{"disambiguationData":[TD([[makeQuery(id+"F0.imprint","IMPRINT",EDGE,{"disambiguationData":[TD([[subQ2,-1.0]])],"derivedFrom":subQ1}),1.0]])]});}
            var Q71;
            {var subQ0=sQuery(id+"F0.wireOp",EDGE,"E14.0");var subQ1=sQuery(id+"F0.wireOp",EDGE,"E0");var subQ2=makeQuery(id+"F0.imprint","INTERSECT",VERTEX,{"disambiguationData":[OD(1.0)],"derivedFrom":[subQ1,subQ0]});Q71=makeQuery(id+"F0.imprint","IMPRINT",FACE,{"disambiguationData":[TD([[makeQuery(id+"F0.imprint","IMPRINT",EDGE,{"disambiguationData":[TD([[subQ2,-1.0]])],"derivedFrom":subQ1}),1.0]])]});}
            var Q72;
            {var subQ0=sQuery(id+"F0.wireOp",EDGE,"E19.0");var subQ1=sQuery(id+"F0.wireOp",EDGE,"E0");var subQ2=makeQuery(id+"F0.imprint","INTERSECT",VERTEX,{"disambiguationData":[OD(1.0)],"derivedFrom":[subQ1,subQ0]});Q72=makeQuery(id+"F0.imprint","IMPRINT",FACE,{"disambiguationData":[TD([[makeQuery(id+"F0.imprint","IMPRINT",EDGE,{"disambiguationData":[TD([[subQ2,-1.0]])],"derivedFrom":subQ1}),1.0]])]});}
            var Q73;
            {var subQ0=sQuery(id+"F0.wireOp",EDGE,"E3.6.0.0");var subQ1=sQuery(id+"F0.wireOp",EDGE,"E0");var subQ2=makeQuery(id+"F0.imprint","INTERSECT",VERTEX,{"disambiguationData":[OD(0.0)],"derivedFrom":[subQ1,subQ0]});Q73=makeQuery(id+"F0.imprint","IMPRINT",FACE,{"disambiguationData":[TD([[makeQuery(id+"F0.imprint","IMPRINT",EDGE,{"disambiguationData":[TD([[subQ2,-1.0]])],"derivedFrom":subQ1}),1.0]])]});}
            var Q74;
            {var subQ0=sQuery(id+"F0.wireOp",EDGE,"E8.MirrorCS");var subQ1=sQuery(id+"F0.wireOp",EDGE,"E1");var subQ2=makeQuery(id+"F0.imprint","INTERSECT",VERTEX,{"derivedFrom":[subQ1,subQ0]});Q74=makeQuery(id+"F0.imprint","IMPRINT",FACE,{"disambiguationData":[TD([[makeQuery(id+"F0.imprint","IMPRINT",EDGE,{"disambiguationData":[TD([[subQ2,1.0]])],"derivedFrom":subQ1}),1.0]])]});}
            var Q75;
            {var subQ0=sQuery(id+"F0.wireOp",EDGE,"E3.1.0.0");var subQ1=sQuery(id+"F0.wireOp",EDGE,"E1");var subQ2=makeQuery(id+"F0.imprint","INTERSECT",VERTEX,{"derivedFrom":[subQ1,subQ0]});Q75=makeQuery(id+"F0.imprint","IMPRINT",FACE,{"disambiguationData":[TD([[makeQuery(id+"F0.imprint","IMPRINT",EDGE,{"disambiguationData":[TD([[subQ2,1.0]])],"derivedFrom":subQ1}),1.0]])]});}
            var Q76;
            {var subQ0=sQuery(id+"F0.wireOp",EDGE,"E18.0");var subQ1=sQuery(id+"F0.wireOp",EDGE,"E0");var subQ2=makeQuery(id+"F0.imprint","INTERSECT",VERTEX,{"disambiguationData":[OD(0.0)],"derivedFrom":[subQ1,subQ0]});Q76=makeQuery(id+"F0.imprint","IMPRINT",FACE,{"disambiguationData":[TD([[makeQuery(id+"F0.imprint","IMPRINT",EDGE,{"disambiguationData":[TD([[subQ2,-1.0]])],"derivedFrom":subQ1}),1.0]])]});}
            var Q77;
            {var subQ0=sQuery(id+"F0.wireOp",EDGE,"E5.MirrorCS");var subQ1=sQuery(id+"F0.wireOp",EDGE,"E1");var subQ2=makeQuery(id+"F0.imprint","INTERSECT",VERTEX,{"derivedFrom":[subQ1,subQ0]});Q77=makeQuery(id+"F0.imprint","IMPRINT",FACE,{"disambiguationData":[TD([[makeQuery(id+"F0.imprint","IMPRINT",EDGE,{"disambiguationData":[TD([[subQ2,-1.0]])],"derivedFrom":subQ1}),1.0]])]});}
            var Q78;
            {var subQ0=sQuery(id+"F0.wireOp",EDGE,"E4.MirrorCS");var subQ1=sQuery(id+"F0.wireOp",EDGE,"E1");var subQ2=makeQuery(id+"F0.imprint","INTERSECT",VERTEX,{"derivedFrom":[subQ1,subQ0]});Q78=makeQuery(id+"F0.imprint","IMPRINT",FACE,{"disambiguationData":[TD([[makeQuery(id+"F0.imprint","IMPRINT",EDGE,{"disambiguationData":[TD([[subQ2,-1.0]])],"derivedFrom":subQ1}),-1.0]])]});}
            var Q79;
            {var subQ0=sQuery(id+"F0.wireOp",EDGE,"E14.0");var subQ1=sQuery(id+"F0.wireOp",EDGE,"E1");var subQ2=makeQuery(id+"F0.imprint","INTERSECT",VERTEX,{"derivedFrom":[subQ1,subQ0]});Q79=makeQuery(id+"F0.imprint","IMPRINT",FACE,{"disambiguationData":[TD([[makeQuery(id+"F0.imprint","IMPRINT",EDGE,{"disambiguationData":[TD([[subQ2,1.0]])],"derivedFrom":subQ1}),-1.0]])]});}
            var Q80;
            {var subQ0=sQuery(id+"F0.wireOp",EDGE,"E4.MirrorCS");var subQ1=sQuery(id+"F0.wireOp",EDGE,"E0");var subQ2=makeQuery(id+"F0.imprint","INTERSECT",VERTEX,{"disambiguationData":[OD(0.0)],"derivedFrom":[subQ1,subQ0]});Q80=makeQuery(id+"F0.imprint","IMPRINT",FACE,{"disambiguationData":[TD([[makeQuery(id+"F0.imprint","IMPRINT",EDGE,{"disambiguationData":[TD([[subQ2,-1.0]])],"derivedFrom":subQ1}),1.0]])]});}
            var Q81;
            {var subQ0=sQuery(id+"F0.wireOp",EDGE,"E1");var subQ1=sQuery(id+"F0.wireOp",EDGE,"E0");var subQ2=makeQuery(id+"F0.imprint","INTERSECT",VERTEX,{"disambiguationData":[OD(0.0)],"derivedFrom":[subQ1,subQ0]});Q81=makeQuery(id+"F0.imprint","IMPRINT",FACE,{"disambiguationData":[TD([[makeQuery(id+"F0.imprint","IMPRINT",EDGE,{"disambiguationData":[TD([[subQ2,1.0]])],"derivedFrom":subQ1}),1.0]])]});}
            var Q82;
            {var subQ0=sQuery(id+"F0.wireOp",EDGE,"E3.2.0.0");var subQ1=sQuery(id+"F0.wireOp",EDGE,"E1");var subQ2=makeQuery(id+"F0.imprint","INTERSECT",VERTEX,{"derivedFrom":[subQ1,subQ0]});Q82=makeQuery(id+"F0.imprint","IMPRINT",FACE,{"disambiguationData":[TD([[makeQuery(id+"F0.imprint","IMPRINT",EDGE,{"disambiguationData":[TD([[subQ2,-1.0]])],"derivedFrom":subQ1}),1.0]])]});}
            var Q83;
            {var subQ0=sQuery(id+"F0.wireOp",EDGE,"E3.5.0.0");var subQ1=sQuery(id+"F0.wireOp",EDGE,"E0");var subQ2=makeQuery(id+"F0.imprint","INTERSECT",VERTEX,{"disambiguationData":[OD(1.0)],"derivedFrom":[subQ1,subQ0]});Q83=makeQuery(id+"F0.imprint","IMPRINT",FACE,{"disambiguationData":[TD([[makeQuery(id+"F0.imprint","IMPRINT",EDGE,{"disambiguationData":[TD([[subQ2,-1.0]])],"derivedFrom":subQ1}),1.0]])]});}
            var Q84;
            {var subQ0=sQuery(id+"F0.wireOp",EDGE,"E2");var subQ1=sQuery(id+"F0.wireOp",EDGE,"E1");var subQ2=makeQuery(id+"F0.imprint","INTERSECT",VERTEX,{"derivedFrom":[subQ1,subQ0]});Q84=makeQuery(id+"F0.imprint","IMPRINT",FACE,{"disambiguationData":[TD([[makeQuery(id+"F0.imprint","IMPRINT",EDGE,{"disambiguationData":[TD([[subQ2,-1.0]])],"derivedFrom":subQ1}),1.0]])]});}
            var Q85;
            {var subQ0=sQuery(id+"F0.wireOp",EDGE,"E10.0");var subQ1=sQuery(id+"F0.wireOp",EDGE,"E1");var subQ2=makeQuery(id+"F0.imprint","INTERSECT",VERTEX,{"derivedFrom":[subQ1,subQ0]});Q85=makeQuery(id+"F0.imprint","IMPRINT",FACE,{"disambiguationData":[TD([[makeQuery(id+"F0.imprint","IMPRINT",EDGE,{"disambiguationData":[TD([[subQ2,1.0]])],"derivedFrom":subQ1}),-1.0]])]});}
            var Q86;
            {var subQ0=sQuery(id+"F0.wireOp",EDGE,"E3.1.0.0");var subQ1=sQuery(id+"F0.wireOp",EDGE,"E1");var subQ2=makeQuery(id+"F0.imprint","INTERSECT",VERTEX,{"derivedFrom":[subQ1,subQ0]});Q86=makeQuery(id+"F0.imprint","IMPRINT",FACE,{"disambiguationData":[TD([[makeQuery(id+"F0.imprint","IMPRINT",EDGE,{"disambiguationData":[TD([[subQ2,1.0]])],"derivedFrom":subQ1}),-1.0]])]});}
            var Q87;
            {var subQ0=sQuery(id+"F0.wireOp",EDGE,"E1");var subQ1=sQuery(id+"F0.wireOp",EDGE,"E0");var subQ2=makeQuery(id+"F0.imprint","INTERSECT",VERTEX,{"disambiguationData":[OD(0.0)],"derivedFrom":[subQ1,subQ0]});Q87=makeQuery(id+"F0.imprint","IMPRINT",FACE,{"disambiguationData":[TD([[makeQuery(id+"F0.imprint","IMPRINT",EDGE,{"disambiguationData":[TD([[subQ2,-1.0]])],"derivedFrom":subQ1}),1.0]])]});}
            var Q88;
            {var subQ0=sQuery(id+"F0.wireOp",EDGE,"E3.2.0.0");var subQ1=sQuery(id+"F0.wireOp",EDGE,"E1");var subQ2=makeQuery(id+"F0.imprint","INTERSECT",VERTEX,{"derivedFrom":[subQ1,subQ0]});Q88=makeQuery(id+"F0.imprint","IMPRINT",FACE,{"disambiguationData":[TD([[makeQuery(id+"F0.imprint","IMPRINT",EDGE,{"disambiguationData":[TD([[subQ2,1.0]])],"derivedFrom":subQ1}),1.0]])]});}
            var Q89;
            {var subQ0=sQuery(id+"F0.wireOp",EDGE,"E20.0");var subQ1=sQuery(id+"F0.wireOp",EDGE,"E0");var subQ2=makeQuery(id+"F0.imprint","INTERSECT",VERTEX,{"disambiguationData":[OD(0.0)],"derivedFrom":[subQ1,subQ0]});Q89=makeQuery(id+"F0.imprint","IMPRINT",FACE,{"disambiguationData":[TD([[makeQuery(id+"F0.imprint","IMPRINT",EDGE,{"disambiguationData":[TD([[subQ2,-1.0]])],"derivedFrom":subQ1}),1.0]])]});}
            var Q90;
            {var subQ0=sQuery(id+"F0.wireOp",EDGE,"E9.MirrorCS");var subQ1=sQuery(id+"F0.wireOp",EDGE,"E1");var subQ2=makeQuery(id+"F0.imprint","INTERSECT",VERTEX,{"derivedFrom":[subQ1,subQ0]});Q90=makeQuery(id+"F0.imprint","IMPRINT",FACE,{"disambiguationData":[TD([[makeQuery(id+"F0.imprint","IMPRINT",EDGE,{"disambiguationData":[TD([[subQ2,1.0]])],"derivedFrom":subQ1}),1.0]])]});}
            var Q91;
            {var subQ0=sQuery(id+"F0.wireOp",EDGE,"E10.0");var subQ1=sQuery(id+"F0.wireOp",EDGE,"E0");var subQ2=makeQuery(id+"F0.imprint","INTERSECT",VERTEX,{"disambiguationData":[OD(0.0)],"derivedFrom":[subQ1,subQ0]});Q91=makeQuery(id+"F0.imprint","IMPRINT",FACE,{"disambiguationData":[TD([[makeQuery(id+"F0.imprint","IMPRINT",EDGE,{"disambiguationData":[TD([[subQ2,-1.0]])],"derivedFrom":subQ1}),1.0]])]});}
            var Q92;
            {var subQ0=sQuery(id+"F0.wireOp",EDGE,"E19.0");var subQ1=sQuery(id+"F0.wireOp",EDGE,"E0");var subQ2=makeQuery(id+"F0.imprint","INTERSECT",VERTEX,{"disambiguationData":[OD(0.0)],"derivedFrom":[subQ1,subQ0]});Q92=makeQuery(id+"F0.imprint","IMPRINT",FACE,{"disambiguationData":[TD([[makeQuery(id+"F0.imprint","IMPRINT",EDGE,{"disambiguationData":[TD([[subQ2,1.0]])],"derivedFrom":subQ1}),1.0]])]});}
            var Q93;
            {var subQ0=sQuery(id+"F0.wireOp",EDGE,"E3.2.0.0");var subQ1=sQuery(id+"F0.wireOp",EDGE,"E0");var subQ2=makeQuery(id+"F0.imprint","INTERSECT",VERTEX,{"disambiguationData":[OD(1.0)],"derivedFrom":[subQ1,subQ0]});Q93=makeQuery(id+"F0.imprint","IMPRINT",FACE,{"disambiguationData":[TD([[makeQuery(id+"F0.imprint","IMPRINT",EDGE,{"disambiguationData":[TD([[subQ2,-1.0]])],"derivedFrom":subQ1}),1.0]])]});}
            var Q94;
            {var subQ0=sQuery(id+"F0.wireOp",EDGE,"E5.MirrorCS");var subQ1=sQuery(id+"F0.wireOp",EDGE,"E1");var subQ2=makeQuery(id+"F0.imprint","INTERSECT",VERTEX,{"derivedFrom":[subQ1,subQ0]});Q94=makeQuery(id+"F0.imprint","IMPRINT",FACE,{"disambiguationData":[TD([[makeQuery(id+"F0.imprint","IMPRINT",EDGE,{"disambiguationData":[TD([[subQ2,1.0]])],"derivedFrom":subQ1}),1.0]])]});}
            var Q95;
            {var subQ0=sQuery(id+"F0.wireOp",EDGE,"E21.0");var subQ1=sQuery(id+"F0.wireOp",EDGE,"E0");var subQ2=makeQuery(id+"F0.imprint","INTERSECT",VERTEX,{"disambiguationData":[OD(1.0)],"derivedFrom":[subQ1,subQ0]});Q95=makeQuery(id+"F0.imprint","IMPRINT",FACE,{"disambiguationData":[TD([[makeQuery(id+"F0.imprint","IMPRINT",EDGE,{"disambiguationData":[TD([[subQ2,-1.0]])],"derivedFrom":subQ1}),1.0]])]});}
            var Q96;
            {var subQ0=sQuery(id+"F0.wireOp",EDGE,"E9.MirrorCS");var subQ1=sQuery(id+"F0.wireOp",EDGE,"E0");var subQ2=makeQuery(id+"F0.imprint","INTERSECT",VERTEX,{"disambiguationData":[OD(0.0)],"derivedFrom":[subQ1,subQ0]});Q96=makeQuery(id+"F0.imprint","IMPRINT",FACE,{"disambiguationData":[TD([[makeQuery(id+"F0.imprint","IMPRINT",EDGE,{"disambiguationData":[TD([[subQ2,-1.0]])],"derivedFrom":subQ1}),1.0]])]});}
            var Q97;
            {var subQ0=sQuery(id+"F0.wireOp",EDGE,"E14.0");var subQ1=sQuery(id+"F0.wireOp",EDGE,"E1");var subQ2=makeQuery(id+"F0.imprint","INTERSECT",VERTEX,{"derivedFrom":[subQ1,subQ0]});Q97=makeQuery(id+"F0.imprint","IMPRINT",FACE,{"disambiguationData":[TD([[makeQuery(id+"F0.imprint","IMPRINT",EDGE,{"disambiguationData":[TD([[subQ2,1.0]])],"derivedFrom":subQ1}),1.0]])]});}
            var Q98;
            {var subQ0=sQuery(id+"F0.wireOp",EDGE,"E12.0");var subQ1=sQuery(id+"F0.wireOp",EDGE,"E0");var subQ2=makeQuery(id+"F0.imprint","INTERSECT",VERTEX,{"disambiguationData":[OD(0.0)],"derivedFrom":[subQ1,subQ0]});Q98=makeQuery(id+"F0.imprint","IMPRINT",FACE,{"disambiguationData":[TD([[makeQuery(id+"F0.imprint","IMPRINT",EDGE,{"disambiguationData":[TD([[subQ2,-1.0]])],"derivedFrom":subQ1}),1.0]])]});}
            var Q99;
            {var subQ0=sQuery(id+"F0.wireOp",EDGE,"E3.6.0.0");var subQ1=sQuery(id+"F0.wireOp",EDGE,"E1");var subQ2=makeQuery(id+"F0.imprint","INTERSECT",VERTEX,{"derivedFrom":[subQ1,subQ0]});Q99=makeQuery(id+"F0.imprint","IMPRINT",FACE,{"disambiguationData":[TD([[makeQuery(id+"F0.imprint","IMPRINT",EDGE,{"disambiguationData":[TD([[subQ2,1.0]])],"derivedFrom":subQ1}),1.0]])]});}
            var Q100;
            {var subQ0=sQuery(id+"F0.wireOp",EDGE,"E11.0");var subQ1=sQuery(id+"F0.wireOp",EDGE,"E0");var subQ2=makeQuery(id+"F0.imprint","INTERSECT",VERTEX,{"disambiguationData":[OD(0.0)],"derivedFrom":[subQ1,subQ0]});Q100=makeQuery(id+"F0.imprint","IMPRINT",FACE,{"disambiguationData":[TD([[makeQuery(id+"F0.imprint","IMPRINT",EDGE,{"disambiguationData":[TD([[subQ2,1.0]])],"derivedFrom":subQ1}),1.0]])]});}
            var Q101;
            {var subQ0=sQuery(id+"F0.wireOp",EDGE,"E4.MirrorCS");var subQ1=sQuery(id+"F0.wireOp",EDGE,"E1");var subQ2=makeQuery(id+"F0.imprint","INTERSECT",VERTEX,{"derivedFrom":[subQ1,subQ0]});Q101=makeQuery(id+"F0.imprint","IMPRINT",FACE,{"disambiguationData":[TD([[makeQuery(id+"F0.imprint","IMPRINT",EDGE,{"disambiguationData":[TD([[subQ2,-1.0]])],"derivedFrom":subQ1}),1.0]])]});}
            var Q102;
            {var subQ0=sQuery(id+"F0.wireOp",EDGE,"E5.MirrorCS");var subQ1=sQuery(id+"F0.wireOp",EDGE,"E0");var subQ2=makeQuery(id+"F0.imprint","INTERSECT",VERTEX,{"disambiguationData":[OD(1.0)],"derivedFrom":[subQ1,subQ0]});Q102=makeQuery(id+"F0.imprint","IMPRINT",FACE,{"disambiguationData":[TD([[makeQuery(id+"F0.imprint","IMPRINT",EDGE,{"disambiguationData":[TD([[subQ2,-1.0]])],"derivedFrom":subQ1}),1.0]])]});}
            var Q103;
            {var subQ0=sQuery(id+"F0.wireOp",EDGE,"E11.0");var subQ1=sQuery(id+"F0.wireOp",EDGE,"E0");var subQ2=makeQuery(id+"F0.imprint","INTERSECT",VERTEX,{"disambiguationData":[OD(1.0)],"derivedFrom":[subQ1,subQ0]});Q103=makeQuery(id+"F0.imprint","IMPRINT",FACE,{"disambiguationData":[TD([[makeQuery(id+"F0.imprint","IMPRINT",EDGE,{"disambiguationData":[TD([[subQ2,-1.0]])],"derivedFrom":subQ1}),1.0]])]});}
            var Q104;
            {var subQ0=sQuery(id+"F0.wireOp",EDGE,"E16.0");var subQ1=sQuery(id+"F0.wireOp",EDGE,"E0");var subQ2=makeQuery(id+"F0.imprint","INTERSECT",VERTEX,{"disambiguationData":[OD(1.0)],"derivedFrom":[subQ1,subQ0]});Q104=makeQuery(id+"F0.imprint","IMPRINT",FACE,{"disambiguationData":[TD([[makeQuery(id+"F0.imprint","IMPRINT",EDGE,{"disambiguationData":[TD([[subQ2,-1.0]])],"derivedFrom":subQ1}),1.0]])]});}
            var Q105;
            {var subQ0=sQuery(id+"F0.wireOp",EDGE,"E12.0");var subQ1=sQuery(id+"F0.wireOp",EDGE,"E1");var subQ2=makeQuery(id+"F0.imprint","INTERSECT",VERTEX,{"derivedFrom":[subQ1,subQ0]});Q105=makeQuery(id+"F0.imprint","IMPRINT",FACE,{"disambiguationData":[TD([[makeQuery(id+"F0.imprint","IMPRINT",EDGE,{"disambiguationData":[TD([[subQ2,1.0]])],"derivedFrom":subQ1}),1.0]])]});}
            var Q106;
            {var subQ0=sQuery(id+"F0.wireOp",EDGE,"E2");var subQ1=sQuery(id+"F0.wireOp",EDGE,"E1");var subQ2=makeQuery(id+"F0.imprint","INTERSECT",VERTEX,{"derivedFrom":[subQ1,subQ0]});Q106=makeQuery(id+"F0.imprint","IMPRINT",FACE,{"disambiguationData":[TD([[makeQuery(id+"F0.imprint","IMPRINT",EDGE,{"disambiguationData":[TD([[subQ2,1.0]])],"derivedFrom":subQ1}),1.0]])]});}
            var Q107;
            {var subQ0=sQuery(id+"F0.wireOp",EDGE,"E2");var subQ1=sQuery(id+"F0.wireOp",EDGE,"E1");var subQ2=makeQuery(id+"F0.imprint","INTERSECT",VERTEX,{"derivedFrom":[subQ1,subQ0]});Q107=makeQuery(id+"F0.imprint","IMPRINT",FACE,{"disambiguationData":[TD([[makeQuery(id+"F0.imprint","IMPRINT",EDGE,{"disambiguationData":[TD([[subQ2,1.0]])],"derivedFrom":subQ1}),-1.0]])]});}
            extrude(context, id + "F1", {"entities" : qUnion([Q0, Q1, Q2, Q3, Q4, Q5, Q6, Q7, Q8, Q9, Q10, Q11, Q12, Q13, Q14, Q15, Q16, Q17, Q18, Q19, Q20, Q21, Q22, Q23, Q24, Q25, Q26, Q27, Q28, Q29, Q30, Q31, Q32, Q33, Q34, Q35, Q36, Q37, Q38, Q39, Q40, Q41, Q42, Q43, Q44, Q45, Q46, Q47, Q48, Q49, Q50, Q51, Q52, Q53, Q54, Q55, Q56, Q57, Q58, Q59, Q60, Q61, Q62, Q63, Q64, Q65, Q66, Q67, Q68, Q69, Q70, Q71, Q72, Q73, Q74, Q75, Q76, Q77, Q78, Q79, Q80, Q81, Q82, Q83, Q84, Q85, Q86, Q87, Q88, Q89, Q90, Q91, Q92, Q93, Q94, Q95, Q96, Q97, Q98, Q99, Q100, Q101, Q102, Q103, Q104, Q105, Q106, Q107]), "depth" : 25 * mm, "offsetDistance" : 25 * mm});
        }
        {
            var Q0;
            {var subQ0=sQuery(id+"F0.wireOp",EDGE,"E1");var subQ1=sQuery(id+"F0.wireOp",EDGE,"E0");var subQ2=makeQuery(id+"F0.imprint","INTERSECT",VERTEX,{"disambiguationData":[OD(0.0)],"derivedFrom":[subQ1,subQ0]});Q0=makeQuery(id+"F0.imprint","IMPRINT",FACE,{"disambiguationData":[TD([[makeQuery(id+"F0.imprint","IMPRINT",EDGE,{"disambiguationData":[TD([[subQ2,1.0]])],"derivedFrom":subQ1}),1.0]])]});}
            var Q1;
            {var subQ0=sQuery(id+"F0.wireOp",EDGE,"E1");var subQ1=sQuery(id+"F0.wireOp",EDGE,"E0");var subQ2=makeQuery(id+"F0.imprint","INTERSECT",VERTEX,{"disambiguationData":[OD(0.0)],"derivedFrom":[subQ1,subQ0]});Q1=makeQuery(id+"F0.imprint","IMPRINT",FACE,{"disambiguationData":[TD([[makeQuery(id+"F0.imprint","IMPRINT",EDGE,{"disambiguationData":[TD([[subQ2,-1.0]])],"derivedFrom":subQ1}),1.0]])]});}
            var Q2;
            {var subQ0=sQuery(id+"F0.wireOp",EDGE,"E3.6.0.0");var subQ1=sQuery(id+"F0.wireOp",EDGE,"E1");var subQ2=makeQuery(id+"F0.imprint","INTERSECT",VERTEX,{"derivedFrom":[subQ1,subQ0]});Q2=makeQuery(id+"F0.imprint","IMPRINT",FACE,{"disambiguationData":[TD([[makeQuery(id+"F0.imprint","IMPRINT",EDGE,{"disambiguationData":[TD([[subQ2,1.0]])],"derivedFrom":subQ1}),1.0]])]});}
            var Q3;
            {var subQ0=sQuery(id+"F0.wireOp",EDGE,"E3.6.0.0");var subQ1=sQuery(id+"F0.wireOp",EDGE,"E0");var subQ2=makeQuery(id+"F0.imprint","INTERSECT",VERTEX,{"disambiguationData":[OD(0.0)],"derivedFrom":[subQ1,subQ0]});Q3=makeQuery(id+"F0.imprint","IMPRINT",FACE,{"disambiguationData":[TD([[makeQuery(id+"F0.imprint","IMPRINT",EDGE,{"disambiguationData":[TD([[subQ2,-1.0]])],"derivedFrom":subQ1}),1.0]])]});}
            var Q4;
            {var subQ0=sQuery(id+"F0.wireOp",EDGE,"E10.0");var subQ1=sQuery(id+"F0.wireOp",EDGE,"E1");var subQ2=makeQuery(id+"F0.imprint","INTERSECT",VERTEX,{"derivedFrom":[subQ1,subQ0]});Q4=makeQuery(id+"F0.imprint","IMPRINT",FACE,{"disambiguationData":[TD([[makeQuery(id+"F0.imprint","IMPRINT",EDGE,{"disambiguationData":[TD([[subQ2,1.0]])],"derivedFrom":subQ1}),1.0]])]});}
            var Q5;
            {var subQ0=sQuery(id+"F0.wireOp",EDGE,"E10.0");var subQ1=sQuery(id+"F0.wireOp",EDGE,"E1");var subQ2=makeQuery(id+"F0.imprint","INTERSECT",VERTEX,{"derivedFrom":[subQ1,subQ0]});Q5=makeQuery(id+"F0.imprint","IMPRINT",FACE,{"disambiguationData":[TD([[makeQuery(id+"F0.imprint","IMPRINT",EDGE,{"disambiguationData":[TD([[subQ2,1.0]])],"derivedFrom":subQ1}),-1.0]])]});}
            var Q6;
            {var subQ0=sQuery(id+"F0.wireOp",EDGE,"E3.6.0.0");var subQ1=sQuery(id+"F0.wireOp",EDGE,"E1");var subQ2=makeQuery(id+"F0.imprint","INTERSECT",VERTEX,{"derivedFrom":[subQ1,subQ0]});Q6=makeQuery(id+"F0.imprint","IMPRINT",FACE,{"disambiguationData":[TD([[makeQuery(id+"F0.imprint","IMPRINT",EDGE,{"disambiguationData":[TD([[subQ2,1.0]])],"derivedFrom":subQ1}),-1.0]])]});}
            var Q7;
            {var subQ0=sQuery(id+"F0.wireOp",EDGE,"E10.0");var subQ1=sQuery(id+"F0.wireOp",EDGE,"E0");var subQ2=makeQuery(id+"F0.imprint","INTERSECT",VERTEX,{"disambiguationData":[OD(1.0)],"derivedFrom":[subQ1,subQ0]});Q7=makeQuery(id+"F0.imprint","IMPRINT",FACE,{"disambiguationData":[TD([[makeQuery(id+"F0.imprint","IMPRINT",EDGE,{"disambiguationData":[TD([[subQ2,-1.0]])],"derivedFrom":subQ1}),1.0]])]});}
            var Q8;
            {var subQ0=sQuery(id+"F0.wireOp",EDGE,"E11.0");var subQ1=sQuery(id+"F0.wireOp",EDGE,"E1");var subQ2=makeQuery(id+"F0.imprint","INTERSECT",VERTEX,{"derivedFrom":[subQ1,subQ0]});Q8=makeQuery(id+"F0.imprint","IMPRINT",FACE,{"disambiguationData":[TD([[makeQuery(id+"F0.imprint","IMPRINT",EDGE,{"disambiguationData":[TD([[subQ2,-1.0]])],"derivedFrom":subQ1}),-1.0]])]});}
            var Q9;
            {var subQ0=sQuery(id+"F0.wireOp",EDGE,"E11.0");var subQ1=sQuery(id+"F0.wireOp",EDGE,"E0");var subQ2=makeQuery(id+"F0.imprint","INTERSECT",VERTEX,{"disambiguationData":[OD(1.0)],"derivedFrom":[subQ1,subQ0]});Q9=makeQuery(id+"F0.imprint","IMPRINT",FACE,{"disambiguationData":[TD([[makeQuery(id+"F0.imprint","IMPRINT",EDGE,{"disambiguationData":[TD([[subQ2,-1.0]])],"derivedFrom":subQ1}),1.0]])]});}
            var Q10;
            {var subQ0=sQuery(id+"F0.wireOp",EDGE,"E11.0");var subQ1=sQuery(id+"F0.wireOp",EDGE,"E1");var subQ2=makeQuery(id+"F0.imprint","INTERSECT",VERTEX,{"derivedFrom":[subQ1,subQ0]});Q10=makeQuery(id+"F0.imprint","IMPRINT",FACE,{"disambiguationData":[TD([[makeQuery(id+"F0.imprint","IMPRINT",EDGE,{"disambiguationData":[TD([[subQ2,-1.0]])],"derivedFrom":subQ1}),1.0]])]});}
            var Q11;
            {var subQ0=sQuery(id+"F0.wireOp",EDGE,"E11.0");var subQ1=sQuery(id+"F0.wireOp",EDGE,"E1");var subQ2=makeQuery(id+"F0.imprint","INTERSECT",VERTEX,{"derivedFrom":[subQ1,subQ0]});Q11=makeQuery(id+"F0.imprint","IMPRINT",FACE,{"disambiguationData":[TD([[makeQuery(id+"F0.imprint","IMPRINT",EDGE,{"disambiguationData":[TD([[subQ2,1.0]])],"derivedFrom":subQ1}),1.0]])]});}
            var Q12;
            {var subQ0=sQuery(id+"F0.wireOp",EDGE,"E11.0");var subQ1=sQuery(id+"F0.wireOp",EDGE,"E1");var subQ2=makeQuery(id+"F0.imprint","INTERSECT",VERTEX,{"derivedFrom":[subQ1,subQ0]});Q12=makeQuery(id+"F0.imprint","IMPRINT",FACE,{"disambiguationData":[TD([[makeQuery(id+"F0.imprint","IMPRINT",EDGE,{"disambiguationData":[TD([[subQ2,1.0]])],"derivedFrom":subQ1}),-1.0]])]});}
            var Q13;
            {var subQ0=sQuery(id+"F0.wireOp",EDGE,"E11.0");var subQ1=sQuery(id+"F0.wireOp",EDGE,"E0");var subQ2=makeQuery(id+"F0.imprint","INTERSECT",VERTEX,{"disambiguationData":[OD(0.0)],"derivedFrom":[subQ1,subQ0]});Q13=makeQuery(id+"F0.imprint","IMPRINT",FACE,{"disambiguationData":[TD([[makeQuery(id+"F0.imprint","IMPRINT",EDGE,{"disambiguationData":[TD([[subQ2,1.0]])],"derivedFrom":subQ1}),1.0]])]});}
            var Q14;
            {var subQ0=sQuery(id+"F0.wireOp",EDGE,"E12.0");var subQ1=sQuery(id+"F0.wireOp",EDGE,"E1");var subQ2=makeQuery(id+"F0.imprint","INTERSECT",VERTEX,{"derivedFrom":[subQ1,subQ0]});Q14=makeQuery(id+"F0.imprint","IMPRINT",FACE,{"disambiguationData":[TD([[makeQuery(id+"F0.imprint","IMPRINT",EDGE,{"disambiguationData":[TD([[subQ2,-1.0]])],"derivedFrom":subQ1}),1.0]])]});}
            var Q15;
            {var subQ0=sQuery(id+"F0.wireOp",EDGE,"E12.0");var subQ1=sQuery(id+"F0.wireOp",EDGE,"E0");var subQ2=makeQuery(id+"F0.imprint","INTERSECT",VERTEX,{"disambiguationData":[OD(0.0)],"derivedFrom":[subQ1,subQ0]});Q15=makeQuery(id+"F0.imprint","IMPRINT",FACE,{"disambiguationData":[TD([[makeQuery(id+"F0.imprint","IMPRINT",EDGE,{"disambiguationData":[TD([[subQ2,1.0]])],"derivedFrom":subQ1}),1.0]])]});}
            var Q16;
            {var subQ0=sQuery(id+"F0.wireOp",EDGE,"E12.0");var subQ1=sQuery(id+"F0.wireOp",EDGE,"E1");var subQ2=makeQuery(id+"F0.imprint","INTERSECT",VERTEX,{"derivedFrom":[subQ1,subQ0]});Q16=makeQuery(id+"F0.imprint","IMPRINT",FACE,{"disambiguationData":[TD([[makeQuery(id+"F0.imprint","IMPRINT",EDGE,{"disambiguationData":[TD([[subQ2,1.0]])],"derivedFrom":subQ1}),1.0]])]});}
            var Q17;
            {var subQ0=sQuery(id+"F0.wireOp",EDGE,"E12.0");var subQ1=sQuery(id+"F0.wireOp",EDGE,"E1");var subQ2=makeQuery(id+"F0.imprint","INTERSECT",VERTEX,{"derivedFrom":[subQ1,subQ0]});Q17=makeQuery(id+"F0.imprint","IMPRINT",FACE,{"disambiguationData":[TD([[makeQuery(id+"F0.imprint","IMPRINT",EDGE,{"disambiguationData":[TD([[subQ2,1.0]])],"derivedFrom":subQ1}),-1.0]])]});}
            var Q18;
            {var subQ0=sQuery(id+"F0.wireOp",EDGE,"E12.0");var subQ1=sQuery(id+"F0.wireOp",EDGE,"E1");var subQ2=makeQuery(id+"F0.imprint","INTERSECT",VERTEX,{"derivedFrom":[subQ1,subQ0]});Q18=makeQuery(id+"F0.imprint","IMPRINT",FACE,{"disambiguationData":[TD([[makeQuery(id+"F0.imprint","IMPRINT",EDGE,{"disambiguationData":[TD([[subQ2,-1.0]])],"derivedFrom":subQ1}),-1.0]])]});}
            var Q19;
            {var subQ0=sQuery(id+"F0.wireOp",EDGE,"E12.0");var subQ1=sQuery(id+"F0.wireOp",EDGE,"E0");var subQ2=makeQuery(id+"F0.imprint","INTERSECT",VERTEX,{"disambiguationData":[OD(1.0)],"derivedFrom":[subQ1,subQ0]});Q19=makeQuery(id+"F0.imprint","IMPRINT",FACE,{"disambiguationData":[TD([[makeQuery(id+"F0.imprint","IMPRINT",EDGE,{"disambiguationData":[TD([[subQ2,-1.0]])],"derivedFrom":subQ1}),1.0]])]});}
            var Q20;
            {var subQ0=sQuery(id+"F0.wireOp",EDGE,"E13.0");var subQ1=sQuery(id+"F0.wireOp",EDGE,"E1");var subQ2=makeQuery(id+"F0.imprint","INTERSECT",VERTEX,{"derivedFrom":[subQ1,subQ0]});Q20=makeQuery(id+"F0.imprint","IMPRINT",FACE,{"disambiguationData":[TD([[makeQuery(id+"F0.imprint","IMPRINT",EDGE,{"disambiguationData":[TD([[subQ2,-1.0]])],"derivedFrom":subQ1}),-1.0]])]});}
            var Q21;
            {var subQ0=sQuery(id+"F0.wireOp",EDGE,"E13.0");var subQ1=sQuery(id+"F0.wireOp",EDGE,"E1");var subQ2=makeQuery(id+"F0.imprint","INTERSECT",VERTEX,{"derivedFrom":[subQ1,subQ0]});Q21=makeQuery(id+"F0.imprint","IMPRINT",FACE,{"disambiguationData":[TD([[makeQuery(id+"F0.imprint","IMPRINT",EDGE,{"disambiguationData":[TD([[subQ2,-1.0]])],"derivedFrom":subQ1}),1.0]])]});}
            var Q22;
            {var subQ0=sQuery(id+"F0.wireOp",EDGE,"E3.3.0.0");var subQ1=sQuery(id+"F0.wireOp",EDGE,"E0");var subQ2=makeQuery(id+"F0.imprint","INTERSECT",VERTEX,{"disambiguationData":[OD(0.0)],"derivedFrom":[subQ1,subQ0]});Q22=makeQuery(id+"F0.imprint","IMPRINT",FACE,{"disambiguationData":[TD([[makeQuery(id+"F0.imprint","IMPRINT",EDGE,{"disambiguationData":[TD([[subQ2,-1.0]])],"derivedFrom":subQ1}),1.0]])]});}
            var Q23;
            {var subQ0=sQuery(id+"F0.wireOp",EDGE,"E3.2.0.0");var subQ1=sQuery(id+"F0.wireOp",EDGE,"E1");var subQ2=makeQuery(id+"F0.imprint","INTERSECT",VERTEX,{"derivedFrom":[subQ1,subQ0]});Q23=makeQuery(id+"F0.imprint","IMPRINT",FACE,{"disambiguationData":[TD([[makeQuery(id+"F0.imprint","IMPRINT",EDGE,{"disambiguationData":[TD([[subQ2,-1.0]])],"derivedFrom":subQ1}),1.0]])]});}
            var Q24;
            {var subQ0=sQuery(id+"F0.wireOp",EDGE,"E3.2.0.0");var subQ1=sQuery(id+"F0.wireOp",EDGE,"E1");var subQ2=makeQuery(id+"F0.imprint","INTERSECT",VERTEX,{"derivedFrom":[subQ1,subQ0]});Q24=makeQuery(id+"F0.imprint","IMPRINT",FACE,{"disambiguationData":[TD([[makeQuery(id+"F0.imprint","IMPRINT",EDGE,{"disambiguationData":[TD([[subQ2,-1.0]])],"derivedFrom":subQ1}),-1.0]])]});}
            var Q25;
            {var subQ0=sQuery(id+"F0.wireOp",EDGE,"E13.0");var subQ1=sQuery(id+"F0.wireOp",EDGE,"E0");var subQ2=makeQuery(id+"F0.imprint","INTERSECT",VERTEX,{"disambiguationData":[OD(1.0)],"derivedFrom":[subQ1,subQ0]});Q25=makeQuery(id+"F0.imprint","IMPRINT",FACE,{"disambiguationData":[TD([[makeQuery(id+"F0.imprint","IMPRINT",EDGE,{"disambiguationData":[TD([[subQ2,-1.0]])],"derivedFrom":subQ1}),1.0]])]});}
            var Q26;
            {var subQ0=sQuery(id+"F0.wireOp",EDGE,"E3.2.0.0");var subQ1=sQuery(id+"F0.wireOp",EDGE,"E1");var subQ2=makeQuery(id+"F0.imprint","INTERSECT",VERTEX,{"derivedFrom":[subQ1,subQ0]});Q26=makeQuery(id+"F0.imprint","IMPRINT",FACE,{"disambiguationData":[TD([[makeQuery(id+"F0.imprint","IMPRINT",EDGE,{"disambiguationData":[TD([[subQ2,1.0]])],"derivedFrom":subQ1}),-1.0]])]});}
            var Q27;
            {var subQ0=sQuery(id+"F0.wireOp",EDGE,"E3.2.0.0");var subQ1=sQuery(id+"F0.wireOp",EDGE,"E1");var subQ2=makeQuery(id+"F0.imprint","INTERSECT",VERTEX,{"derivedFrom":[subQ1,subQ0]});Q27=makeQuery(id+"F0.imprint","IMPRINT",FACE,{"disambiguationData":[TD([[makeQuery(id+"F0.imprint","IMPRINT",EDGE,{"disambiguationData":[TD([[subQ2,1.0]])],"derivedFrom":subQ1}),1.0]])]});}
            var Q28;
            {var subQ0=sQuery(id+"F0.wireOp",EDGE,"E14.0");var subQ1=sQuery(id+"F0.wireOp",EDGE,"E1");var subQ2=makeQuery(id+"F0.imprint","INTERSECT",VERTEX,{"derivedFrom":[subQ1,subQ0]});Q28=makeQuery(id+"F0.imprint","IMPRINT",FACE,{"disambiguationData":[TD([[makeQuery(id+"F0.imprint","IMPRINT",EDGE,{"disambiguationData":[TD([[subQ2,1.0]])],"derivedFrom":subQ1}),1.0]])]});}
            var Q29;
            {var subQ0=sQuery(id+"F0.wireOp",EDGE,"E14.0");var subQ1=sQuery(id+"F0.wireOp",EDGE,"E1");var subQ2=makeQuery(id+"F0.imprint","INTERSECT",VERTEX,{"derivedFrom":[subQ1,subQ0]});Q29=makeQuery(id+"F0.imprint","IMPRINT",FACE,{"disambiguationData":[TD([[makeQuery(id+"F0.imprint","IMPRINT",EDGE,{"disambiguationData":[TD([[subQ2,1.0]])],"derivedFrom":subQ1}),-1.0]])]});}
            var Q30;
            {var subQ0=sQuery(id+"F0.wireOp",EDGE,"E3.2.0.0");var subQ1=sQuery(id+"F0.wireOp",EDGE,"E0");var subQ2=makeQuery(id+"F0.imprint","INTERSECT",VERTEX,{"disambiguationData":[OD(0.0)],"derivedFrom":[subQ1,subQ0]});Q30=makeQuery(id+"F0.imprint","IMPRINT",FACE,{"disambiguationData":[TD([[makeQuery(id+"F0.imprint","IMPRINT",EDGE,{"disambiguationData":[TD([[subQ2,-1.0]])],"derivedFrom":subQ1}),1.0]])]});}
            var Q31;
            {var subQ0=sQuery(id+"F0.wireOp",EDGE,"E14.0");var subQ1=sQuery(id+"F0.wireOp",EDGE,"E0");var subQ2=makeQuery(id+"F0.imprint","INTERSECT",VERTEX,{"disambiguationData":[OD(1.0)],"derivedFrom":[subQ1,subQ0]});Q31=makeQuery(id+"F0.imprint","IMPRINT",FACE,{"disambiguationData":[TD([[makeQuery(id+"F0.imprint","IMPRINT",EDGE,{"disambiguationData":[TD([[subQ2,-1.0]])],"derivedFrom":subQ1}),1.0]])]});}
            var Q32;
            {var subQ0=sQuery(id+"F0.wireOp",EDGE,"E3.1.0.0");var subQ1=sQuery(id+"F0.wireOp",EDGE,"E1");var subQ2=makeQuery(id+"F0.imprint","INTERSECT",VERTEX,{"derivedFrom":[subQ1,subQ0]});Q32=makeQuery(id+"F0.imprint","IMPRINT",FACE,{"disambiguationData":[TD([[makeQuery(id+"F0.imprint","IMPRINT",EDGE,{"disambiguationData":[TD([[subQ2,1.0]])],"derivedFrom":subQ1}),-1.0]])]});}
            var Q33;
            {var subQ0=sQuery(id+"F0.wireOp",EDGE,"E3.1.0.0");var subQ1=sQuery(id+"F0.wireOp",EDGE,"E1");var subQ2=makeQuery(id+"F0.imprint","INTERSECT",VERTEX,{"derivedFrom":[subQ1,subQ0]});Q33=makeQuery(id+"F0.imprint","IMPRINT",FACE,{"disambiguationData":[TD([[makeQuery(id+"F0.imprint","IMPRINT",EDGE,{"disambiguationData":[TD([[subQ2,1.0]])],"derivedFrom":subQ1}),1.0]])]});}
            var Q34;
            {var subQ0=sQuery(id+"F0.wireOp",EDGE,"E2");var subQ1=sQuery(id+"F0.wireOp",EDGE,"E1");var subQ2=makeQuery(id+"F0.imprint","INTERSECT",VERTEX,{"derivedFrom":[subQ1,subQ0]});Q34=makeQuery(id+"F0.imprint","IMPRINT",FACE,{"disambiguationData":[TD([[makeQuery(id+"F0.imprint","IMPRINT",EDGE,{"disambiguationData":[TD([[subQ2,-1.0]])],"derivedFrom":subQ1}),1.0]])]});}
            var Q35;
            {var subQ0=sQuery(id+"F0.wireOp",EDGE,"E2");var subQ1=sQuery(id+"F0.wireOp",EDGE,"E1");var subQ2=makeQuery(id+"F0.imprint","INTERSECT",VERTEX,{"derivedFrom":[subQ1,subQ0]});Q35=makeQuery(id+"F0.imprint","IMPRINT",FACE,{"disambiguationData":[TD([[makeQuery(id+"F0.imprint","IMPRINT",EDGE,{"disambiguationData":[TD([[subQ2,-1.0]])],"derivedFrom":subQ1}),-1.0]])]});}
            var Q36;
            {var subQ0=sQuery(id+"F0.wireOp",EDGE,"E15.0");var subQ1=sQuery(id+"F0.wireOp",EDGE,"E0");var subQ2=makeQuery(id+"F0.imprint","INTERSECT",VERTEX,{"disambiguationData":[OD(0.0)],"derivedFrom":[subQ1,subQ0]});Q36=makeQuery(id+"F0.imprint","IMPRINT",FACE,{"disambiguationData":[TD([[makeQuery(id+"F0.imprint","IMPRINT",EDGE,{"disambiguationData":[TD([[subQ2,1.0]])],"derivedFrom":subQ1}),1.0]])]});}
            var Q37;
            {var subQ0=sQuery(id+"F0.wireOp",EDGE,"E15.0");var subQ1=sQuery(id+"F0.wireOp",EDGE,"E0");var subQ2=makeQuery(id+"F0.imprint","INTERSECT",VERTEX,{"disambiguationData":[OD(1.0)],"derivedFrom":[subQ1,subQ0]});Q37=makeQuery(id+"F0.imprint","IMPRINT",FACE,{"disambiguationData":[TD([[makeQuery(id+"F0.imprint","IMPRINT",EDGE,{"disambiguationData":[TD([[subQ2,-1.0]])],"derivedFrom":subQ1}),1.0]])]});}
            var Q38;
            {var subQ0=sQuery(id+"F0.wireOp",EDGE,"E2");var subQ1=sQuery(id+"F0.wireOp",EDGE,"E1");var subQ2=makeQuery(id+"F0.imprint","INTERSECT",VERTEX,{"derivedFrom":[subQ1,subQ0]});Q38=makeQuery(id+"F0.imprint","IMPRINT",FACE,{"disambiguationData":[TD([[makeQuery(id+"F0.imprint","IMPRINT",EDGE,{"disambiguationData":[TD([[subQ2,1.0]])],"derivedFrom":subQ1}),-1.0]])]});}
            var Q39;
            {var subQ0=sQuery(id+"F0.wireOp",EDGE,"E4.MirrorCS");var subQ1=sQuery(id+"F0.wireOp",EDGE,"E1");var subQ2=makeQuery(id+"F0.imprint","INTERSECT",VERTEX,{"derivedFrom":[subQ1,subQ0]});Q39=makeQuery(id+"F0.imprint","IMPRINT",FACE,{"disambiguationData":[TD([[makeQuery(id+"F0.imprint","IMPRINT",EDGE,{"disambiguationData":[TD([[subQ2,-1.0]])],"derivedFrom":subQ1}),-1.0]])]});}
            var Q40;
            {var subQ0=sQuery(id+"F0.wireOp",EDGE,"E4.MirrorCS");var subQ1=sQuery(id+"F0.wireOp",EDGE,"E1");var subQ2=makeQuery(id+"F0.imprint","INTERSECT",VERTEX,{"derivedFrom":[subQ1,subQ0]});Q40=makeQuery(id+"F0.imprint","IMPRINT",FACE,{"disambiguationData":[TD([[makeQuery(id+"F0.imprint","IMPRINT",EDGE,{"disambiguationData":[TD([[subQ2,-1.0]])],"derivedFrom":subQ1}),1.0]])]});}
            var Q41;
            {var subQ0=sQuery(id+"F0.wireOp",EDGE,"E2");var subQ1=sQuery(id+"F0.wireOp",EDGE,"E1");var subQ2=makeQuery(id+"F0.imprint","INTERSECT",VERTEX,{"derivedFrom":[subQ1,subQ0]});Q41=makeQuery(id+"F0.imprint","IMPRINT",FACE,{"disambiguationData":[TD([[makeQuery(id+"F0.imprint","IMPRINT",EDGE,{"disambiguationData":[TD([[subQ2,1.0]])],"derivedFrom":subQ1}),1.0]])]});}
            var Q42;
            {var subQ0=sQuery(id+"F0.wireOp",EDGE,"E2");var subQ1=sQuery(id+"F0.wireOp",EDGE,"E0");var subQ2=makeQuery(id+"F0.imprint","INTERSECT",VERTEX,{"disambiguationData":[OD(0.0)],"derivedFrom":[subQ1,subQ0]});Q42=makeQuery(id+"F0.imprint","IMPRINT",FACE,{"disambiguationData":[TD([[makeQuery(id+"F0.imprint","IMPRINT",EDGE,{"disambiguationData":[TD([[subQ2,-1.0]])],"derivedFrom":subQ1}),1.0]])]});}
            var Q43;
            {var subQ0=sQuery(id+"F0.wireOp",EDGE,"E16.0");var subQ1=sQuery(id+"F0.wireOp",EDGE,"E0");var subQ2=makeQuery(id+"F0.imprint","INTERSECT",VERTEX,{"disambiguationData":[OD(1.0)],"derivedFrom":[subQ1,subQ0]});Q43=makeQuery(id+"F0.imprint","IMPRINT",FACE,{"disambiguationData":[TD([[makeQuery(id+"F0.imprint","IMPRINT",EDGE,{"disambiguationData":[TD([[subQ2,-1.0]])],"derivedFrom":subQ1}),1.0]])]});}
            var Q44;
            {var subQ0=sQuery(id+"F0.wireOp",EDGE,"E17.0");var subQ1=sQuery(id+"F0.wireOp",EDGE,"E1");var subQ2=makeQuery(id+"F0.imprint","INTERSECT",VERTEX,{"derivedFrom":[subQ1,subQ0]});Q44=makeQuery(id+"F0.imprint","IMPRINT",FACE,{"disambiguationData":[TD([[makeQuery(id+"F0.imprint","IMPRINT",EDGE,{"disambiguationData":[TD([[subQ2,-1.0]])],"derivedFrom":subQ1}),-1.0]])]});}
            var Q45;
            {var subQ0=sQuery(id+"F0.wireOp",EDGE,"E17.0");var subQ1=sQuery(id+"F0.wireOp",EDGE,"E0");var subQ2=makeQuery(id+"F0.imprint","INTERSECT",VERTEX,{"disambiguationData":[OD(1.0)],"derivedFrom":[subQ1,subQ0]});Q45=makeQuery(id+"F0.imprint","IMPRINT",FACE,{"disambiguationData":[TD([[makeQuery(id+"F0.imprint","IMPRINT",EDGE,{"disambiguationData":[TD([[subQ2,-1.0]])],"derivedFrom":subQ1}),1.0]])]});}
            var Q46;
            {var subQ0=sQuery(id+"F0.wireOp",EDGE,"E5.MirrorCS");var subQ1=sQuery(id+"F0.wireOp",EDGE,"E1");var subQ2=makeQuery(id+"F0.imprint","INTERSECT",VERTEX,{"derivedFrom":[subQ1,subQ0]});Q46=makeQuery(id+"F0.imprint","IMPRINT",FACE,{"disambiguationData":[TD([[makeQuery(id+"F0.imprint","IMPRINT",EDGE,{"disambiguationData":[TD([[subQ2,-1.0]])],"derivedFrom":subQ1}),-1.0]])]});}
            var Q47;
            {var subQ0=sQuery(id+"F0.wireOp",EDGE,"E5.MirrorCS");var subQ1=sQuery(id+"F0.wireOp",EDGE,"E1");var subQ2=makeQuery(id+"F0.imprint","INTERSECT",VERTEX,{"derivedFrom":[subQ1,subQ0]});Q47=makeQuery(id+"F0.imprint","IMPRINT",FACE,{"disambiguationData":[TD([[makeQuery(id+"F0.imprint","IMPRINT",EDGE,{"disambiguationData":[TD([[subQ2,-1.0]])],"derivedFrom":subQ1}),1.0]])]});}
            var Q48;
            {var subQ0=sQuery(id+"F0.wireOp",EDGE,"E17.0");var subQ1=sQuery(id+"F0.wireOp",EDGE,"E1");var subQ2=makeQuery(id+"F0.imprint","INTERSECT",VERTEX,{"derivedFrom":[subQ1,subQ0]});Q48=makeQuery(id+"F0.imprint","IMPRINT",FACE,{"disambiguationData":[TD([[makeQuery(id+"F0.imprint","IMPRINT",EDGE,{"disambiguationData":[TD([[subQ2,-1.0]])],"derivedFrom":subQ1}),1.0]])]});}
            var Q49;
            {var subQ0=sQuery(id+"F0.wireOp",EDGE,"E4.MirrorCS");var subQ1=sQuery(id+"F0.wireOp",EDGE,"E0");var subQ2=makeQuery(id+"F0.imprint","INTERSECT",VERTEX,{"disambiguationData":[OD(0.0)],"derivedFrom":[subQ1,subQ0]});Q49=makeQuery(id+"F0.imprint","IMPRINT",FACE,{"disambiguationData":[TD([[makeQuery(id+"F0.imprint","IMPRINT",EDGE,{"disambiguationData":[TD([[subQ2,-1.0]])],"derivedFrom":subQ1}),1.0]])]});}
            var Q50;
            {var subQ0=sQuery(id+"F0.wireOp",EDGE,"E5.MirrorCS");var subQ1=sQuery(id+"F0.wireOp",EDGE,"E0");var subQ2=makeQuery(id+"F0.imprint","INTERSECT",VERTEX,{"disambiguationData":[OD(0.0)],"derivedFrom":[subQ1,subQ0]});Q50=makeQuery(id+"F0.imprint","IMPRINT",FACE,{"disambiguationData":[TD([[makeQuery(id+"F0.imprint","IMPRINT",EDGE,{"disambiguationData":[TD([[subQ2,-1.0]])],"derivedFrom":subQ1}),1.0]])]});}
            var Q51;
            {var subQ0=sQuery(id+"F0.wireOp",EDGE,"E5.MirrorCS");var subQ1=sQuery(id+"F0.wireOp",EDGE,"E1");var subQ2=makeQuery(id+"F0.imprint","INTERSECT",VERTEX,{"derivedFrom":[subQ1,subQ0]});Q51=makeQuery(id+"F0.imprint","IMPRINT",FACE,{"disambiguationData":[TD([[makeQuery(id+"F0.imprint","IMPRINT",EDGE,{"disambiguationData":[TD([[subQ2,1.0]])],"derivedFrom":subQ1}),1.0]])]});}
            var Q52;
            {var subQ0=sQuery(id+"F0.wireOp",EDGE,"E6.MirrorCS");var subQ1=sQuery(id+"F0.wireOp",EDGE,"E1");var subQ2=makeQuery(id+"F0.imprint","INTERSECT",VERTEX,{"derivedFrom":[subQ1,subQ0]});Q52=makeQuery(id+"F0.imprint","IMPRINT",FACE,{"disambiguationData":[TD([[makeQuery(id+"F0.imprint","IMPRINT",EDGE,{"disambiguationData":[TD([[subQ2,-1.0]])],"derivedFrom":subQ1}),1.0]])]});}
            var Q53;
            {var subQ0=sQuery(id+"F0.wireOp",EDGE,"E6.MirrorCS");var subQ1=sQuery(id+"F0.wireOp",EDGE,"E1");var subQ2=makeQuery(id+"F0.imprint","INTERSECT",VERTEX,{"derivedFrom":[subQ1,subQ0]});Q53=makeQuery(id+"F0.imprint","IMPRINT",FACE,{"disambiguationData":[TD([[makeQuery(id+"F0.imprint","IMPRINT",EDGE,{"disambiguationData":[TD([[subQ2,-1.0]])],"derivedFrom":subQ1}),-1.0]])]});}
            var Q54;
            {var subQ0=sQuery(id+"F0.wireOp",EDGE,"E5.MirrorCS");var subQ1=sQuery(id+"F0.wireOp",EDGE,"E1");var subQ2=makeQuery(id+"F0.imprint","INTERSECT",VERTEX,{"derivedFrom":[subQ1,subQ0]});Q54=makeQuery(id+"F0.imprint","IMPRINT",FACE,{"disambiguationData":[TD([[makeQuery(id+"F0.imprint","IMPRINT",EDGE,{"disambiguationData":[TD([[subQ2,1.0]])],"derivedFrom":subQ1}),-1.0]])]});}
            var Q55;
            {var subQ0=sQuery(id+"F0.wireOp",EDGE,"E18.0");var subQ1=sQuery(id+"F0.wireOp",EDGE,"E0");var subQ2=makeQuery(id+"F0.imprint","INTERSECT",VERTEX,{"disambiguationData":[OD(1.0)],"derivedFrom":[subQ1,subQ0]});Q55=makeQuery(id+"F0.imprint","IMPRINT",FACE,{"disambiguationData":[TD([[makeQuery(id+"F0.imprint","IMPRINT",EDGE,{"disambiguationData":[TD([[subQ2,-1.0]])],"derivedFrom":subQ1}),1.0]])]});}
            var Q56;
            {var subQ0=sQuery(id+"F0.wireOp",EDGE,"E6.MirrorCS");var subQ1=sQuery(id+"F0.wireOp",EDGE,"E1");var subQ2=makeQuery(id+"F0.imprint","INTERSECT",VERTEX,{"derivedFrom":[subQ1,subQ0]});Q56=makeQuery(id+"F0.imprint","IMPRINT",FACE,{"disambiguationData":[TD([[makeQuery(id+"F0.imprint","IMPRINT",EDGE,{"disambiguationData":[TD([[subQ2,1.0]])],"derivedFrom":subQ1}),-1.0]])]});}
            var Q57;
            {var subQ0=sQuery(id+"F0.wireOp",EDGE,"E19.0");var subQ1=sQuery(id+"F0.wireOp",EDGE,"E0");var subQ2=makeQuery(id+"F0.imprint","INTERSECT",VERTEX,{"disambiguationData":[OD(1.0)],"derivedFrom":[subQ1,subQ0]});Q57=makeQuery(id+"F0.imprint","IMPRINT",FACE,{"disambiguationData":[TD([[makeQuery(id+"F0.imprint","IMPRINT",EDGE,{"disambiguationData":[TD([[subQ2,-1.0]])],"derivedFrom":subQ1}),1.0]])]});}
            var Q58;
            {var subQ0=sQuery(id+"F0.wireOp",EDGE,"E7.MirrorCS");var subQ1=sQuery(id+"F0.wireOp",EDGE,"E1");var subQ2=makeQuery(id+"F0.imprint","INTERSECT",VERTEX,{"derivedFrom":[subQ1,subQ0]});Q58=makeQuery(id+"F0.imprint","IMPRINT",FACE,{"disambiguationData":[TD([[makeQuery(id+"F0.imprint","IMPRINT",EDGE,{"disambiguationData":[TD([[subQ2,-1.0]])],"derivedFrom":subQ1}),-1.0]])]});}
            var Q59;
            {var subQ0=sQuery(id+"F0.wireOp",EDGE,"E6.MirrorCS");var subQ1=sQuery(id+"F0.wireOp",EDGE,"E1");var subQ2=makeQuery(id+"F0.imprint","INTERSECT",VERTEX,{"derivedFrom":[subQ1,subQ0]});Q59=makeQuery(id+"F0.imprint","IMPRINT",FACE,{"disambiguationData":[TD([[makeQuery(id+"F0.imprint","IMPRINT",EDGE,{"disambiguationData":[TD([[subQ2,1.0]])],"derivedFrom":subQ1}),1.0]])]});}
            var Q60;
            {var subQ0=sQuery(id+"F0.wireOp",EDGE,"E19.0");var subQ1=sQuery(id+"F0.wireOp",EDGE,"E0");var subQ2=makeQuery(id+"F0.imprint","INTERSECT",VERTEX,{"disambiguationData":[OD(0.0)],"derivedFrom":[subQ1,subQ0]});Q60=makeQuery(id+"F0.imprint","IMPRINT",FACE,{"disambiguationData":[TD([[makeQuery(id+"F0.imprint","IMPRINT",EDGE,{"disambiguationData":[TD([[subQ2,1.0]])],"derivedFrom":subQ1}),1.0]])]});}
            var Q61;
            {var subQ0=sQuery(id+"F0.wireOp",EDGE,"E7.MirrorCS");var subQ1=sQuery(id+"F0.wireOp",EDGE,"E1");var subQ2=makeQuery(id+"F0.imprint","INTERSECT",VERTEX,{"derivedFrom":[subQ1,subQ0]});Q61=makeQuery(id+"F0.imprint","IMPRINT",FACE,{"disambiguationData":[TD([[makeQuery(id+"F0.imprint","IMPRINT",EDGE,{"disambiguationData":[TD([[subQ2,-1.0]])],"derivedFrom":subQ1}),1.0]])]});}
            var Q62;
            {var subQ0=sQuery(id+"F0.wireOp",EDGE,"E7.MirrorCS");var subQ1=sQuery(id+"F0.wireOp",EDGE,"E1");var subQ2=makeQuery(id+"F0.imprint","INTERSECT",VERTEX,{"derivedFrom":[subQ1,subQ0]});Q62=makeQuery(id+"F0.imprint","IMPRINT",FACE,{"disambiguationData":[TD([[makeQuery(id+"F0.imprint","IMPRINT",EDGE,{"disambiguationData":[TD([[subQ2,1.0]])],"derivedFrom":subQ1}),1.0]])]});}
            var Q63;
            {var subQ0=sQuery(id+"F0.wireOp",EDGE,"E8.MirrorCS");var subQ1=sQuery(id+"F0.wireOp",EDGE,"E1");var subQ2=makeQuery(id+"F0.imprint","INTERSECT",VERTEX,{"derivedFrom":[subQ1,subQ0]});Q63=makeQuery(id+"F0.imprint","IMPRINT",FACE,{"disambiguationData":[TD([[makeQuery(id+"F0.imprint","IMPRINT",EDGE,{"disambiguationData":[TD([[subQ2,-1.0]])],"derivedFrom":subQ1}),1.0]])]});}
            var Q64;
            {var subQ0=sQuery(id+"F0.wireOp",EDGE,"E7.MirrorCS");var subQ1=sQuery(id+"F0.wireOp",EDGE,"E1");var subQ2=makeQuery(id+"F0.imprint","INTERSECT",VERTEX,{"derivedFrom":[subQ1,subQ0]});Q64=makeQuery(id+"F0.imprint","IMPRINT",FACE,{"disambiguationData":[TD([[makeQuery(id+"F0.imprint","IMPRINT",EDGE,{"disambiguationData":[TD([[subQ2,1.0]])],"derivedFrom":subQ1}),-1.0]])]});}
            var Q65;
            {var subQ0=sQuery(id+"F0.wireOp",EDGE,"E20.0");var subQ1=sQuery(id+"F0.wireOp",EDGE,"E0");var subQ2=makeQuery(id+"F0.imprint","INTERSECT",VERTEX,{"disambiguationData":[OD(1.0)],"derivedFrom":[subQ1,subQ0]});Q65=makeQuery(id+"F0.imprint","IMPRINT",FACE,{"disambiguationData":[TD([[makeQuery(id+"F0.imprint","IMPRINT",EDGE,{"disambiguationData":[TD([[subQ2,-1.0]])],"derivedFrom":subQ1}),1.0]])]});}
            var Q66;
            {var subQ0=sQuery(id+"F0.wireOp",EDGE,"E20.0");var subQ1=sQuery(id+"F0.wireOp",EDGE,"E0");var subQ2=makeQuery(id+"F0.imprint","INTERSECT",VERTEX,{"disambiguationData":[OD(0.0)],"derivedFrom":[subQ1,subQ0]});Q66=makeQuery(id+"F0.imprint","IMPRINT",FACE,{"disambiguationData":[TD([[makeQuery(id+"F0.imprint","IMPRINT",EDGE,{"disambiguationData":[TD([[subQ2,1.0]])],"derivedFrom":subQ1}),1.0]])]});}
            var Q67;
            {var subQ0=sQuery(id+"F0.wireOp",EDGE,"E8.MirrorCS");var subQ1=sQuery(id+"F0.wireOp",EDGE,"E1");var subQ2=makeQuery(id+"F0.imprint","INTERSECT",VERTEX,{"derivedFrom":[subQ1,subQ0]});Q67=makeQuery(id+"F0.imprint","IMPRINT",FACE,{"disambiguationData":[TD([[makeQuery(id+"F0.imprint","IMPRINT",EDGE,{"disambiguationData":[TD([[subQ2,1.0]])],"derivedFrom":subQ1}),1.0]])]});}
            var Q68;
            {var subQ0=sQuery(id+"F0.wireOp",EDGE,"E9.MirrorCS");var subQ1=sQuery(id+"F0.wireOp",EDGE,"E1");var subQ2=makeQuery(id+"F0.imprint","INTERSECT",VERTEX,{"derivedFrom":[subQ1,subQ0]});Q68=makeQuery(id+"F0.imprint","IMPRINT",FACE,{"disambiguationData":[TD([[makeQuery(id+"F0.imprint","IMPRINT",EDGE,{"disambiguationData":[TD([[subQ2,-1.0]])],"derivedFrom":subQ1}),1.0]])]});}
            var Q69;
            {var subQ0=sQuery(id+"F0.wireOp",EDGE,"E8.MirrorCS");var subQ1=sQuery(id+"F0.wireOp",EDGE,"E1");var subQ2=makeQuery(id+"F0.imprint","INTERSECT",VERTEX,{"derivedFrom":[subQ1,subQ0]});Q69=makeQuery(id+"F0.imprint","IMPRINT",FACE,{"disambiguationData":[TD([[makeQuery(id+"F0.imprint","IMPRINT",EDGE,{"disambiguationData":[TD([[subQ2,-1.0]])],"derivedFrom":subQ1}),-1.0]])]});}
            var Q70;
            {var subQ0=sQuery(id+"F0.wireOp",EDGE,"E8.MirrorCS");var subQ1=sQuery(id+"F0.wireOp",EDGE,"E1");var subQ2=makeQuery(id+"F0.imprint","INTERSECT",VERTEX,{"derivedFrom":[subQ1,subQ0]});Q70=makeQuery(id+"F0.imprint","IMPRINT",FACE,{"disambiguationData":[TD([[makeQuery(id+"F0.imprint","IMPRINT",EDGE,{"disambiguationData":[TD([[subQ2,1.0]])],"derivedFrom":subQ1}),-1.0]])]});}
            var Q71;
            {var subQ0=sQuery(id+"F0.wireOp",EDGE,"E21.0");var subQ1=sQuery(id+"F0.wireOp",EDGE,"E0");var subQ2=makeQuery(id+"F0.imprint","INTERSECT",VERTEX,{"disambiguationData":[OD(1.0)],"derivedFrom":[subQ1,subQ0]});Q71=makeQuery(id+"F0.imprint","IMPRINT",FACE,{"disambiguationData":[TD([[makeQuery(id+"F0.imprint","IMPRINT",EDGE,{"disambiguationData":[TD([[subQ2,-1.0]])],"derivedFrom":subQ1}),1.0]])]});}
            var Q72;
            {var subQ0=sQuery(id+"F0.wireOp",EDGE,"E8.MirrorCS");var subQ1=sQuery(id+"F0.wireOp",EDGE,"E0");var subQ2=makeQuery(id+"F0.imprint","INTERSECT",VERTEX,{"disambiguationData":[OD(0.0)],"derivedFrom":[subQ1,subQ0]});Q72=makeQuery(id+"F0.imprint","IMPRINT",FACE,{"disambiguationData":[TD([[makeQuery(id+"F0.imprint","IMPRINT",EDGE,{"disambiguationData":[TD([[subQ2,-1.0]])],"derivedFrom":subQ1}),1.0]])]});}
            var Q73;
            {var subQ0=sQuery(id+"F0.wireOp",EDGE,"E9.MirrorCS");var subQ1=sQuery(id+"F0.wireOp",EDGE,"E1");var subQ2=makeQuery(id+"F0.imprint","INTERSECT",VERTEX,{"derivedFrom":[subQ1,subQ0]});Q73=makeQuery(id+"F0.imprint","IMPRINT",FACE,{"disambiguationData":[TD([[makeQuery(id+"F0.imprint","IMPRINT",EDGE,{"disambiguationData":[TD([[subQ2,-1.0]])],"derivedFrom":subQ1}),-1.0]])]});}
            var Q74;
            {var subQ0=sQuery(id+"F0.wireOp",EDGE,"E9.MirrorCS");var subQ1=sQuery(id+"F0.wireOp",EDGE,"E1");var subQ2=makeQuery(id+"F0.imprint","INTERSECT",VERTEX,{"derivedFrom":[subQ1,subQ0]});Q74=makeQuery(id+"F0.imprint","IMPRINT",FACE,{"disambiguationData":[TD([[makeQuery(id+"F0.imprint","IMPRINT",EDGE,{"disambiguationData":[TD([[subQ2,1.0]])],"derivedFrom":subQ1}),1.0]])]});}
            var Q75;
            {var subQ0=sQuery(id+"F0.wireOp",EDGE,"E9.MirrorCS");var subQ1=sQuery(id+"F0.wireOp",EDGE,"E0");var subQ2=makeQuery(id+"F0.imprint","INTERSECT",VERTEX,{"disambiguationData":[OD(0.0)],"derivedFrom":[subQ1,subQ0]});Q75=makeQuery(id+"F0.imprint","IMPRINT",FACE,{"disambiguationData":[TD([[makeQuery(id+"F0.imprint","IMPRINT",EDGE,{"disambiguationData":[TD([[subQ2,-1.0]])],"derivedFrom":subQ1}),1.0]])]});}
            var Q76;
            {var subQ0=sQuery(id+"F0.wireOp",EDGE,"E23.bottom");var subQ1=sQuery(id+"F0.wireOp",EDGE,"E0");var subQ2=makeQuery(id+"F0.imprint","INTERSECT",VERTEX,{"disambiguationData":[OD(1.0)],"derivedFrom":[subQ1,subQ0]});Q76=makeQuery(id+"F0.imprint","IMPRINT",FACE,{"disambiguationData":[TD([[makeQuery(id+"F0.imprint","IMPRINT",EDGE,{"disambiguationData":[TD([[subQ2,-1.0]])],"derivedFrom":subQ1}),1.0]])]});}
            var Q77;
            {var subQ0=sQuery(id+"F0.wireOp",EDGE,"E23.top");var subQ1=sQuery(id+"F0.wireOp",EDGE,"E0");var subQ2=makeQuery(id+"F0.imprint","INTERSECT",VERTEX,{"disambiguationData":[OD(0.0)],"derivedFrom":[subQ1,subQ0]});Q77=makeQuery(id+"F0.imprint","IMPRINT",FACE,{"disambiguationData":[TD([[makeQuery(id+"F0.imprint","IMPRINT",EDGE,{"disambiguationData":[TD([[subQ2,1.0]])],"derivedFrom":subQ1}),1.0]])]});}
            var Q78;
            {var subQ0=sQuery(id+"F0.wireOp",EDGE,"E9.MirrorCS");var subQ1=sQuery(id+"F0.wireOp",EDGE,"E1");var subQ2=makeQuery(id+"F0.imprint","INTERSECT",VERTEX,{"derivedFrom":[subQ1,subQ0]});Q78=makeQuery(id+"F0.imprint","IMPRINT",FACE,{"disambiguationData":[TD([[makeQuery(id+"F0.imprint","IMPRINT",EDGE,{"disambiguationData":[TD([[subQ2,1.0]])],"derivedFrom":subQ1}),-1.0]])]});}
            var Q79;
            {var subQ0=sQuery(id+"F0.wireOp",EDGE,"E22.0");var subQ1=sQuery(id+"F0.wireOp",EDGE,"E0");var subQ2=makeQuery(id+"F0.imprint","INTERSECT",VERTEX,{"disambiguationData":[OD(1.0)],"derivedFrom":[subQ1,subQ0]});Q79=makeQuery(id+"F0.imprint","IMPRINT",FACE,{"disambiguationData":[TD([[makeQuery(id+"F0.imprint","IMPRINT",EDGE,{"disambiguationData":[TD([[subQ2,-1.0]])],"derivedFrom":subQ1}),1.0]])]});}
            extrude(context, id + "F2", {"entities" : qUnion([Q0, Q1, Q2, Q3, Q4, Q5, Q6, Q7, Q8, Q9, Q10, Q11, Q12, Q13, Q14, Q15, Q16, Q17, Q18, Q19, Q20, Q21, Q22, Q23, Q24, Q25, Q26, Q27, Q28, Q29, Q30, Q31, Q32, Q33, Q34, Q35, Q36, Q37, Q38, Q39, Q40, Q41, Q42, Q43, Q44, Q45, Q46, Q47, Q48, Q49, Q50, Q51, Q52, Q53, Q54, Q55, Q56, Q57, Q58, Q59, Q60, Q61, Q62, Q63, Q64, Q65, Q66, Q67, Q68, Q69, Q70, Q71, Q72, Q73, Q74, Q75, Q76, Q77, Q78, Q79]), "operationType" : NewBodyOperationType.ADD, "depth" : 75 * mm, "offsetDistance" : 25 * mm});
        }
        {
            var Q0;
            {var subQ0=sQuery(id+"F0.wireOp",EDGE,"E22.0");var subQ1=sQuery(id+"F0.wireOp",EDGE,"E0");Q0=makeQuery(id+"F2.opExtrude","SWEPT_EDGE",EDGE,{"disambiguationData":[OSD([subQ1,subQ0]),TDD([makeQuery(id+"F0.imprint","INTERSECT",VERTEX,{"disambiguationData":[OD(1.0)],"derivedFrom":[subQ1,subQ0]})])]});}
            var Q1;
            {var subQ0=sQuery(id+"F0.wireOp",EDGE,"E21.0");var subQ1=sQuery(id+"F0.wireOp",EDGE,"E0");Q1=makeQuery(id+"F2.opExtrude","SWEPT_EDGE",EDGE,{"disambiguationData":[OSD([subQ1,subQ0]),TDD([makeQuery(id+"F0.imprint","INTERSECT",VERTEX,{"disambiguationData":[OD(1.0)],"derivedFrom":[subQ1,subQ0]})])]});}
            var Q2;
            {var subQ0=sQuery(id+"F0.wireOp",EDGE,"E8.MirrorCS");var subQ1=sQuery(id+"F0.wireOp",EDGE,"E0");Q2=makeQuery(id+"F2.opExtrude","SWEPT_EDGE",EDGE,{"disambiguationData":[OSD([subQ1,subQ0]),TDD([makeQuery(id+"F0.imprint","INTERSECT",VERTEX,{"disambiguationData":[OD(1.0)],"derivedFrom":[subQ1,subQ0]})])]});}
            var Q3;
            {var subQ0=sQuery(id+"F0.wireOp",EDGE,"E20.0");var subQ1=sQuery(id+"F0.wireOp",EDGE,"E0");Q3=makeQuery(id+"F2.opExtrude","SWEPT_EDGE",EDGE,{"disambiguationData":[OSD([subQ1,subQ0]),TDD([makeQuery(id+"F0.imprint","INTERSECT",VERTEX,{"disambiguationData":[OD(1.0)],"derivedFrom":[subQ1,subQ0]})])]});}
            var Q4;
            {var subQ0=sQuery(id+"F0.wireOp",EDGE,"E7.MirrorCS");var subQ1=sQuery(id+"F0.wireOp",EDGE,"E0");Q4=makeQuery(id+"F2.opExtrude","SWEPT_EDGE",EDGE,{"disambiguationData":[OSD([subQ1,subQ0]),TDD([makeQuery(id+"F0.imprint","INTERSECT",VERTEX,{"disambiguationData":[OD(1.0)],"derivedFrom":[subQ1,subQ0]})])]});}
            var Q5;
            {var subQ0=sQuery(id+"F0.wireOp",EDGE,"E19.0");var subQ1=sQuery(id+"F0.wireOp",EDGE,"E0");Q5=makeQuery(id+"F2.opExtrude","SWEPT_EDGE",EDGE,{"disambiguationData":[OSD([subQ1,subQ0]),TDD([makeQuery(id+"F0.imprint","INTERSECT",VERTEX,{"disambiguationData":[OD(1.0)],"derivedFrom":[subQ1,subQ0]})])]});}
            var Q6;
            {var subQ0=sQuery(id+"F0.wireOp",EDGE,"E6.MirrorCS");var subQ1=sQuery(id+"F0.wireOp",EDGE,"E0");Q6=makeQuery(id+"F2.opExtrude","SWEPT_EDGE",EDGE,{"disambiguationData":[OSD([subQ1,subQ0]),TDD([makeQuery(id+"F0.imprint","INTERSECT",VERTEX,{"disambiguationData":[OD(1.0)],"derivedFrom":[subQ1,subQ0]})])]});}
            var Q7;
            {var subQ0=sQuery(id+"F0.wireOp",EDGE,"E18.0");var subQ1=sQuery(id+"F0.wireOp",EDGE,"E0");Q7=makeQuery(id+"F2.opExtrude","SWEPT_EDGE",EDGE,{"disambiguationData":[OSD([subQ1,subQ0]),TDD([makeQuery(id+"F0.imprint","INTERSECT",VERTEX,{"disambiguationData":[OD(1.0)],"derivedFrom":[subQ1,subQ0]})])]});}
            var Q8;
            {var subQ0=sQuery(id+"F0.wireOp",EDGE,"E5.MirrorCS");var subQ1=sQuery(id+"F0.wireOp",EDGE,"E0");Q8=makeQuery(id+"F2.opExtrude","SWEPT_EDGE",EDGE,{"disambiguationData":[OSD([subQ1,subQ0]),TDD([makeQuery(id+"F0.imprint","INTERSECT",VERTEX,{"disambiguationData":[OD(1.0)],"derivedFrom":[subQ1,subQ0]})])]});}
            var Q9;
            {var subQ0=sQuery(id+"F0.wireOp",EDGE,"E17.0");var subQ1=sQuery(id+"F0.wireOp",EDGE,"E0");Q9=makeQuery(id+"F2.opExtrude","SWEPT_EDGE",EDGE,{"disambiguationData":[OSD([subQ1,subQ0]),TDD([makeQuery(id+"F0.imprint","INTERSECT",VERTEX,{"disambiguationData":[OD(1.0)],"derivedFrom":[subQ1,subQ0]})])]});}
            var Q10;
            {var subQ0=sQuery(id+"F0.wireOp",EDGE,"E4.MirrorCS");var subQ1=sQuery(id+"F0.wireOp",EDGE,"E0");Q10=makeQuery(id+"F2.opExtrude","SWEPT_EDGE",EDGE,{"disambiguationData":[OSD([subQ1,subQ0]),TDD([makeQuery(id+"F0.imprint","INTERSECT",VERTEX,{"disambiguationData":[OD(1.0)],"derivedFrom":[subQ1,subQ0]})])]});}
            var Q11;
            {var subQ0=sQuery(id+"F0.wireOp",EDGE,"E16.0");var subQ1=sQuery(id+"F0.wireOp",EDGE,"E0");Q11=makeQuery(id+"F2.opExtrude","SWEPT_EDGE",EDGE,{"disambiguationData":[OSD([subQ1,subQ0]),TDD([makeQuery(id+"F0.imprint","INTERSECT",VERTEX,{"disambiguationData":[OD(1.0)],"derivedFrom":[subQ1,subQ0]})])]});}
            var Q12;
            {var subQ0=sQuery(id+"F0.wireOp",EDGE,"E2");var subQ1=sQuery(id+"F0.wireOp",EDGE,"E0");Q12=makeQuery(id+"F2.opExtrude","SWEPT_EDGE",EDGE,{"disambiguationData":[OSD([subQ1,subQ0]),TDD([makeQuery(id+"F0.imprint","INTERSECT",VERTEX,{"disambiguationData":[OD(1.0)],"derivedFrom":[subQ1,subQ0]})])]});}
            var Q13;
            {var subQ0=sQuery(id+"F0.wireOp",EDGE,"E15.0");var subQ1=sQuery(id+"F0.wireOp",EDGE,"E0");Q13=makeQuery(id+"F2.opExtrude","SWEPT_EDGE",EDGE,{"disambiguationData":[OSD([subQ1,subQ0]),TDD([makeQuery(id+"F0.imprint","INTERSECT",VERTEX,{"disambiguationData":[OD(1.0)],"derivedFrom":[subQ1,subQ0]})])]});}
            var Q14;
            {var subQ0=sQuery(id+"F0.wireOp",EDGE,"E3.1.0.0");var subQ1=sQuery(id+"F0.wireOp",EDGE,"E0");Q14=makeQuery(id+"F2.opExtrude","SWEPT_EDGE",EDGE,{"disambiguationData":[OSD([subQ1,subQ0]),TDD([makeQuery(id+"F0.imprint","INTERSECT",VERTEX,{"disambiguationData":[OD(1.0)],"derivedFrom":[subQ1,subQ0]})])]});}
            var Q15;
            {var subQ0=sQuery(id+"F0.wireOp",EDGE,"E14.0");var subQ1=sQuery(id+"F0.wireOp",EDGE,"E0");Q15=makeQuery(id+"F2.opExtrude","SWEPT_EDGE",EDGE,{"disambiguationData":[OSD([subQ1,subQ0]),TDD([makeQuery(id+"F0.imprint","INTERSECT",VERTEX,{"disambiguationData":[OD(1.0)],"derivedFrom":[subQ1,subQ0]})])]});}
            var Q16;
            {var subQ0=sQuery(id+"F0.wireOp",EDGE,"E3.2.0.0");var subQ1=sQuery(id+"F0.wireOp",EDGE,"E0");Q16=makeQuery(id+"F2.opExtrude","SWEPT_EDGE",EDGE,{"disambiguationData":[OSD([subQ1,subQ0]),TDD([makeQuery(id+"F0.imprint","INTERSECT",VERTEX,{"disambiguationData":[OD(1.0)],"derivedFrom":[subQ1,subQ0]})])]});}
            var Q17;
            {var subQ0=sQuery(id+"F0.wireOp",EDGE,"E13.0");var subQ1=sQuery(id+"F0.wireOp",EDGE,"E0");Q17=makeQuery(id+"F2.opExtrude","SWEPT_EDGE",EDGE,{"disambiguationData":[OSD([subQ1,subQ0]),TDD([makeQuery(id+"F0.imprint","INTERSECT",VERTEX,{"disambiguationData":[OD(1.0)],"derivedFrom":[subQ1,subQ0]})])]});}
            var Q18;
            {var subQ0=sQuery(id+"F0.wireOp",EDGE,"E3.3.0.0");var subQ1=sQuery(id+"F0.wireOp",EDGE,"E0");Q18=makeQuery(id+"F2.opExtrude","SWEPT_EDGE",EDGE,{"disambiguationData":[OSD([subQ1,subQ0]),TDD([makeQuery(id+"F0.imprint","INTERSECT",VERTEX,{"disambiguationData":[OD(1.0)],"derivedFrom":[subQ1,subQ0]})])]});}
            var Q19;
            {var subQ0=sQuery(id+"F0.wireOp",EDGE,"E12.0");var subQ1=sQuery(id+"F0.wireOp",EDGE,"E0");Q19=makeQuery(id+"F2.opExtrude","SWEPT_EDGE",EDGE,{"disambiguationData":[OSD([subQ1,subQ0]),TDD([makeQuery(id+"F0.imprint","INTERSECT",VERTEX,{"disambiguationData":[OD(1.0)],"derivedFrom":[subQ1,subQ0]})])]});}
            var Q20;
            {var subQ0=sQuery(id+"F0.wireOp",EDGE,"E3.4.0.0");var subQ1=sQuery(id+"F0.wireOp",EDGE,"E0");Q20=makeQuery(id+"F2.opExtrude","SWEPT_EDGE",EDGE,{"disambiguationData":[OSD([subQ1,subQ0]),TDD([makeQuery(id+"F0.imprint","INTERSECT",VERTEX,{"disambiguationData":[OD(1.0)],"derivedFrom":[subQ1,subQ0]})])]});}
            var Q21;
            {var subQ0=sQuery(id+"F0.wireOp",EDGE,"E3.5.0.0");var subQ1=sQuery(id+"F0.wireOp",EDGE,"E0");Q21=makeQuery(id+"F2.opExtrude","SWEPT_EDGE",EDGE,{"disambiguationData":[OSD([subQ1,subQ0]),TDD([makeQuery(id+"F0.imprint","INTERSECT",VERTEX,{"disambiguationData":[OD(1.0)],"derivedFrom":[subQ1,subQ0]})])]});}
            var Q22;
            {var subQ0=sQuery(id+"F0.wireOp",EDGE,"E3.6.0.0");var subQ1=sQuery(id+"F0.wireOp",EDGE,"E0");Q22=makeQuery(id+"F2.opExtrude","SWEPT_EDGE",EDGE,{"disambiguationData":[OSD([subQ1,subQ0]),TDD([makeQuery(id+"F0.imprint","INTERSECT",VERTEX,{"disambiguationData":[OD(1.0)],"derivedFrom":[subQ1,subQ0]})])]});}
            var Q23;
            {var subQ0=sQuery(id+"F0.wireOp",EDGE,"E11.0");var subQ1=sQuery(id+"F0.wireOp",EDGE,"E0");Q23=makeQuery(id+"F2.opExtrude","SWEPT_EDGE",EDGE,{"disambiguationData":[OSD([subQ1,subQ0]),TDD([makeQuery(id+"F0.imprint","INTERSECT",VERTEX,{"disambiguationData":[OD(1.0)],"derivedFrom":[subQ1,subQ0]})])]});}
            var Q24;
            {var subQ0=sQuery(id+"F0.wireOp",EDGE,"E9.MirrorCS");var subQ1=sQuery(id+"F0.wireOp",EDGE,"E0");Q24=makeQuery(id+"F2.opExtrude","SWEPT_EDGE",EDGE,{"disambiguationData":[OSD([subQ1,subQ0]),TDD([makeQuery(id+"F0.imprint","INTERSECT",VERTEX,{"disambiguationData":[OD(1.0)],"derivedFrom":[subQ1,subQ0]})])]});}
            var Q25;
            {var subQ0=sQuery(id+"F0.wireOp",EDGE,"E10.0");var subQ1=sQuery(id+"F0.wireOp",EDGE,"E0");Q25=makeQuery(id+"F2.opExtrude","SWEPT_EDGE",EDGE,{"disambiguationData":[OSD([subQ1,subQ0]),TDD([makeQuery(id+"F0.imprint","INTERSECT",VERTEX,{"disambiguationData":[OD(1.0)],"derivedFrom":[subQ1,subQ0]})])]});}
            var Q26;
            {var subQ0=sQuery(id+"F0.wireOp",EDGE,"E23.top");var subQ1=sQuery(id+"F0.wireOp",EDGE,"E0");Q26=makeQuery(id+"F2.opExtrude","SWEPT_EDGE",EDGE,{"disambiguationData":[OSD([subQ1,subQ0]),TDD([makeQuery(id+"F0.imprint","INTERSECT",VERTEX,{"disambiguationData":[OD(1.0)],"derivedFrom":[subQ1,subQ0]})])]});}
            var Q27;
            {var subQ0=sQuery(id+"F0.wireOp",EDGE,"E23.bottom");var subQ1=sQuery(id+"F0.wireOp",EDGE,"E0");Q27=makeQuery(id+"F2.opExtrude","SWEPT_EDGE",EDGE,{"disambiguationData":[OSD([subQ1,subQ0]),TDD([makeQuery(id+"F0.imprint","INTERSECT",VERTEX,{"disambiguationData":[OD(0.0)],"derivedFrom":[subQ1,subQ0]})])]});}
            var Q28;
            {var subQ0=sQuery(id+"F0.wireOp",EDGE,"E23.top");var subQ1=sQuery(id+"F0.wireOp",EDGE,"E0");Q28=makeQuery(id+"F2.opExtrude","SWEPT_EDGE",EDGE,{"disambiguationData":[OSD([subQ1,subQ0]),TDD([makeQuery(id+"F0.imprint","INTERSECT",VERTEX,{"disambiguationData":[OD(0.0)],"derivedFrom":[subQ1,subQ0]})])]});}
            var Q29;
            {var subQ0=sQuery(id+"F0.wireOp",EDGE,"E23.bottom");var subQ1=sQuery(id+"F0.wireOp",EDGE,"E0");Q29=makeQuery(id+"F2.opExtrude","SWEPT_EDGE",EDGE,{"disambiguationData":[OSD([subQ1,subQ0]),TDD([makeQuery(id+"F0.imprint","INTERSECT",VERTEX,{"disambiguationData":[OD(1.0)],"derivedFrom":[subQ1,subQ0]})])]});}
            fillet(context, id + "F3", {"entities" : qUnion([Q0, Q1, Q2, Q3, Q4, Q5, Q6, Q7, Q8, Q9, Q10, Q11, Q12, Q13, Q14, Q15, Q16, Q17, Q18, Q19, Q20, Q21, Q22, Q23, Q24, Q25, Q26, Q27, Q28, Q29]), "tangentPropagation" : true, "radius" : 0.5 * mm, "defaultsChanged" : false, "vertexSettings" : [], "allowEdgeOverflow" : false});
        }
    });
